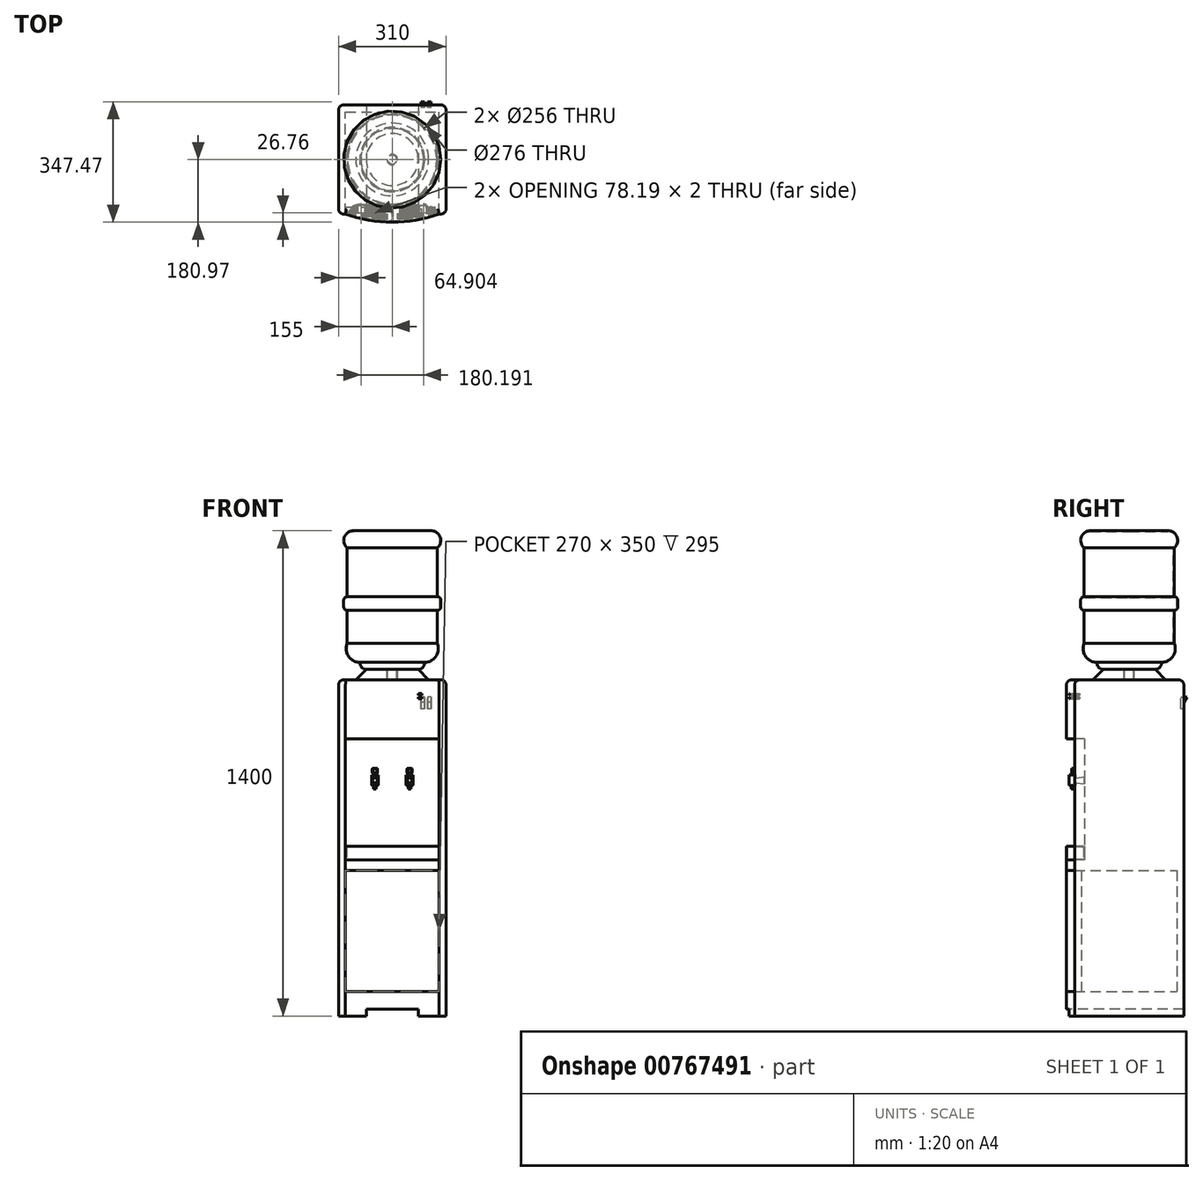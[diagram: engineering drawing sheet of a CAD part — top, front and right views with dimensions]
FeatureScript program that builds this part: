
annotation { "Feature Type Name" : "Feature", "Feature Type Description" : "" }
export const myFeature = defineFeature(function(context is Context, id is Id, definition is map)
    precondition{}
    {
        {
            var Q0;
            Q0=qCreatedBy(makeId("Top.planeOp"),FACE);
            var sketch = newSketch(context, id + "F0", { "sketchPlane" : qUnion([Q0])});
            skLineSegment(sketch, "E0.bottom", {"start": v(155, -157.5) * mm, "end": v(-155, -157.5) * mm});
            skLineSegment(sketch, "E0.top", {"start": v(155, 157.5) * mm, "end": v(-155, 157.5) * mm});
            skLineSegment(sketch, "E0.left", {"start": v(155, -157.5) * mm, "end": v(155, 157.5) * mm});
            skLineSegment(sketch, "E0.right", {"start": v(-155, -157.5) * mm, "end": v(-155, 157.5) * mm});
            skPoint(sketch, "E0.middle", {"position": v(0, 0) * mm});
            skArc(sketch, "E1", {"start": v(-135, -157.5) * mm, "mid": v(0, -180.97) * mm, "end": v(135, -157.5) * mm});
            skSolve(sketch);
        }
        {
            var Q0;
            Q0=makeQuery(id+"F0.imprint","IMPRINT",FACE,{"disambiguationData":[TD([[makeQuery(id+"F0.imprint","IMPRINT",EDGE,{"derivedFrom":sQuery(id+"F0.wireOp",EDGE,"E0.bottom")}),-1.0]])]});
            var Q1;
            {var subQ0=sQuery(id+"F0.wireOp",EDGE,"E1");Q1=makeQuery(id+"F0.imprint","IMPRINT",FACE,{"disambiguationData":[TD([[makeQuery(id+"F0.imprint","IMPRINT",EDGE,{"derivedFrom":subQ0}),1.0]])]});}
            extrude(context, id + "F1", {"entities" : qUnion([Q0, Q1]), "depth" : 970 * mm, "offsetDistance" : 25 * mm});
        }
        {
            var Q0;
            Q0=qCreatedBy(makeId("Front.planeOp"),FACE);
            var sketch = newSketch(context, id + "F2", { "sketchPlane" : qUnion([Q0])});
            skLineSegment(sketch, "E2.0", {"start": v(155, 970) * mm, "end": v(-155, 970) * mm});
            skLineSegment(sketch, "E3", {"start": v(105, 970) * mm, "end": v(75, 1000) * mm});
            skLineSegment(sketch, "E4", {"start": v(75, 1000) * mm, "end": v(0, 1000) * mm});
            skLineSegment(sketch, "E5", {"start": v(0, 1000) * mm, "end": v(0, 970) * mm});
            skLineSegment(sketch, "E6", {"start": v(15, 1000) * mm, "end": v(15, 970) * mm});
            skSolve(sketch);
        }
        {
            var Q0;
            {var subQ0=sQuery(id+"F2.wireOp",EDGE,"E3");Q0=makeQuery(id+"F2.imprint","IMPRINT",FACE,{"disambiguationData":[TD([[makeQuery(id+"F2.imprint","IMPRINT",EDGE,{"derivedFrom":subQ0}),1.0]])]});}
            var Q1;
            Q1=sQuery(id+"F2.wireOp",EDGE,"E5");
            revolve(context, id + "F3", {"operationType" : NewBodyOperationType.ADD, "surfaceOperationType" : NewSurfaceOperationType.NEW, "entities" : qUnion([Q0]), "axis" : qUnion([Q1]), "revolveType" : RevolveType.FULL});
        }
        {
            var Q0;
            Q0=qCreatedBy(makeId("Top.planeOp"),FACE);
            cPlane(context, id + "F4", {"entities" : qUnion([Q0]), "cplaneType" : CPlaneType.OFFSET, "offset" : 450 * mm, "width" : 150 * mm, "height" : 150 * mm});
        }
        {
            var Q0;
            Q0=qCreatedBy(id+"F4.planeOp",FACE);
            var sketch = newSketch(context, id + "F5", { "sketchPlane" : qUnion([Q0])});
            skArc(sketch, "E7.0.0", {"start": v(-135, -157.5) * mm, "mid": v(0, -180.97) * mm, "end": v(135, -157.5) * mm});
            skArc(sketch, "E7.0.2", {"start": v(135, -157.5) * mm, "mid": v(0, -180.97) * mm, "end": v(-135, -157.5) * mm});
            skLineSegment(sketch, "E8", {"start": v(-90, -129.3) * mm, "end": v(0, -129.3) * mm});
            skArc(sketch, "E9", {"start": v(-90, -129.3) * mm, "mid": v(-116.55, -136.93) * mm, "end": v(-135, -157.5) * mm});
            skLineSegment(sketch, "E10.MirrorCS", {"start": v(90, -129.3) * mm, "end": v(0, -129.3) * mm});
            skArc(sketch, "E11.MirrorCS", {"start": v(90, -129.3) * mm, "mid": v(116.55, -136.93) * mm, "end": v(135, -157.5) * mm});
            skSolve(sketch);
        }
        {
            var Q0;
            Q0=qSketchRegion(id+"F5",true);
            extrude(context, id + "F6", {"entities" : qUnion([Q0]), "operationType" : NewBodyOperationType.REMOVE, "depth" : 350 * mm, "offsetDistance" : 25 * mm});
        }
        {
            var Q0;
            Q0=qCreatedBy(makeId("Front.planeOp"),FACE);
            var sketch = newSketch(context, id + "F7", { "sketchPlane" : qUnion([Q0])});
            skLineSegment(sketch, "E12.0", {"start": v(-135, 450) * mm, "end": v(-135, 0) * mm});
            skLineSegment(sketch, "E12.1", {"start": v(135, 450) * mm, "end": v(135, 0) * mm});
            skLineSegment(sketch, "E13", {"start": v(-135, 420) * mm, "end": v(135, 420) * mm});
            skLineSegment(sketch, "E14", {"start": v(-135, 70) * mm, "end": v(135, 70) * mm});
            skSolve(sketch);
        }
        {
            var Q0;
            Q0=qSketchRegion(id+"F7",true);
            extrude(context, id + "F8", {"entities" : qUnion([Q0]), "operationType" : NewBodyOperationType.REMOVE, "endBound" : BoundingType.THROUGH_ALL, "depth" : 25 * mm, "offsetDistance" : 25 * mm, "hasSecondDirection" : true, "secondDirectionOppositeDirection" : true, "secondDirectionDepth" : (315 / 2 - 20) * mm});
        }
        {
            var Q0;
            Q0=qCreatedBy(makeId("Front.planeOp"),FACE);
            var sketch = newSketch(context, id + "F9", { "sketchPlane" : qUnion([Q0])});
            skLineSegment(sketch, "E15.bottom", {"start": v(-75, 20) * mm, "end": v(75, 20) * mm});
            skLineSegment(sketch, "E15.top", {"start": v(-75, 0) * mm, "end": v(75, 0) * mm});
            skLineSegment(sketch, "E15.left", {"start": v(-75, 20) * mm, "end": v(-75, 0) * mm});
            skLineSegment(sketch, "E15.right", {"start": v(75, 20) * mm, "end": v(75, 0) * mm});
            skSolve(sketch);
        }
        {
            var Q0;
            Q0=qSketchRegion(id+"F9",true);
            extrude(context, id + "F10", {"entities" : qUnion([Q0]), "operationType" : NewBodyOperationType.REMOVE, "endBound" : BoundingType.THROUGH_ALL, "oppositeDirection" : true, "depth" : 25 * mm, "offsetDistance" : 25 * mm, "hasSecondDirection" : true, "secondDirectionBound" : BoundingType.THROUGH_ALL, "secondDirectionOppositeDirection" : false, "secondDirectionDepth" : 25 * mm});
        }
        {
            var Q0;
            Q0=qCreatedBy(makeId("Front.planeOp"),FACE);
            var sketch = newSketch(context, id + "F11", { "sketchPlane" : qUnion([Q0])});
            skLineSegment(sketch, "E16.0", {"start": v(-15, 1000) * mm, "end": v(15, 1000) * mm});
            skLineSegment(sketch, "E17.0.0", {"start": v(-15, 970) * mm, "end": v(15, 970) * mm});
            skLineSegment(sketch, "E18", {"start": v(-15, 970) * mm, "end": v(-15, 1000) * mm});
            skLineSegment(sketch, "E19", {"start": v(0, 1400) * mm, "end": v(-112, 1400) * mm});
            skLineSegment(sketch, "E20", {"start": v(-130, 1350.55) * mm, "end": v(-130, 1210) * mm});
            skLineSegment(sketch, "E21", {"start": v(-130, 1170) * mm, "end": v(-130, 1075) * mm});
            skLineSegment(sketch, "E22.0", {"start": v(-75, 1000) * mm, "end": v(75, 1000) * mm});
            skArc(sketch, "E23", {"start": v(-92.88, 1020.1) * mm, "mid": v(-88.45, 1006.04) * mm, "end": v(-75, 1000) * mm});
            skLineSegment(sketch, "E24", {"start": v(-140, 1200) * mm, "end": v(-140, 1180) * mm});
            skArc(sketch, "E25", {"start": v(-140, 1180) * mm, "mid": v(-137.07, 1172.93) * mm, "end": v(-130, 1170) * mm});
            skLineSegment(sketch, "E26", {"start": v(-140, 1180) * mm, "end": v(-130, 1180) * mm, "construction": true});
            skLineSegment(sketch, "E27", {"start": v(-130, 1170) * mm, "end": v(-130, 1180) * mm, "construction": true});
            skArc(sketch, "E28", {"start": v(-112, 1400) * mm, "mid": v(-138.31, 1381.58) * mm, "end": v(-130, 1350.55) * mm});
            skArc(sketch, "E29", {"start": v(-130, 1210) * mm, "mid": v(-137.07, 1207.07) * mm, "end": v(-140, 1200) * mm});
            skLineSegment(sketch, "E30", {"start": v(-140, 1200) * mm, "end": v(-130, 1200) * mm, "construction": true});
            skLineSegment(sketch, "E31", {"start": v(-130, 1210) * mm, "end": v(-130, 1200) * mm, "construction": true});
            skArc(sketch, "E32", {"start": v(-130, 1075) * mm, "mid": v(-126.01, 1037.7) * mm, "end": v(-92.88, 1020.1) * mm});
            skLineSegment(sketch, "E33", {"start": v(-92.88, 1020.1) * mm, "end": v(0, 1020.1) * mm});
            skLineSegment(sketch, "E34", {"start": v(0, 1400) * mm, "end": v(0, 970) * mm});
            skLineSegment(sketch, "E35.0", {"start": v(-75, 1002) * mm, "end": v(75, 1002) * mm});
            skArc(sketch, "E35.1", {"start": v(-90.44, 1022.18) * mm, "mid": v(-87.7, 1008.28) * mm, "end": v(-75, 1002) * mm});
            skArc(sketch, "E35.2", {"start": v(-128, 1074.6) * mm, "mid": v(-123.77, 1037.98) * mm, "end": v(-90.44, 1022.18) * mm});
            skLineSegment(sketch, "E35.3", {"start": v(-128, 1172.25) * mm, "end": v(-128, 1074.6) * mm});
            skArc(sketch, "E35.4", {"start": v(-138, 1180) * mm, "mid": v(-134.9, 1173.68) * mm, "end": v(-128, 1172.25) * mm});
            skLineSegment(sketch, "E35.5", {"start": v(-138, 1200) * mm, "end": v(-138, 1180) * mm});
            skLineSegment(sketch, "E35.6", {"start": v(0, 1398) * mm, "end": v(-112, 1398) * mm});
            skArc(sketch, "E35.7", {"start": v(-112, 1398) * mm, "mid": v(-136.58, 1380.46) * mm, "end": v(-128, 1351.5) * mm});
            skLineSegment(sketch, "E35.8", {"start": v(-128, 1351.5) * mm, "end": v(-128, 1207.75) * mm});
            skArc(sketch, "E35.9", {"start": v(-128, 1207.75) * mm, "mid": v(-134.9, 1206.32) * mm, "end": v(-138, 1200) * mm});
            skLineSegment(sketch, "E36", {"start": v(-13, 970) * mm, "end": v(-13, 1002) * mm});
            skSolve(sketch);
        }
        {
            var Q0;
            {var subQ3=sQuery(id+"F11.wireOp",EDGE,"E18");Q0=makeQuery(id+"F11.imprint","IMPRINT",FACE,{"disambiguationData":[TD([[makeQuery(id+"F11.imprint","IMPRINT",EDGE,{"derivedFrom":subQ3}),-1.0]])]});}
            var Q1;
            {var subQ0=sQuery(id+"F11.wireOp",EDGE,"E23");Q1=makeQuery(id+"F11.imprint","IMPRINT",FACE,{"disambiguationData":[TD([[makeQuery(id+"F11.imprint","IMPRINT",EDGE,{"derivedFrom":subQ0}),1.0]])]});}
            var Q2;
            {var subQ4=sQuery(id+"F11.wireOp",EDGE,"E19");Q2=makeQuery(id+"F11.imprint","IMPRINT",FACE,{"disambiguationData":[TD([[makeQuery(id+"F11.imprint","IMPRINT",EDGE,{"derivedFrom":subQ4}),1.0]])]});}
            var Q3;
            Q3=sQuery(id+"F11.wireOp",EDGE,"E34");
            revolve(context, id + "F12", {"surfaceOperationType" : NewSurfaceOperationType.NEW, "entities" : qUnion([Q0, Q1, Q2]), "axis" : qUnion([Q3]), "revolveType" : RevolveType.FULL});
        }
        {
            var Q0;
            Q0=makeQuery(id+"F1.opExtrude","SWEPT_EDGE",EDGE,{"disambiguationData":[OSD([sQuery(id+"F0.wireOp",EDGE,"E0.top"),sQuery(id+"F0.wireOp",EDGE,"E0.right")])]});
            var Q1;
            Q1=makeQuery(id+"F1.opExtrude","SWEPT_EDGE",EDGE,{"disambiguationData":[OSD([sQuery(id+"F0.wireOp",EDGE,"E0.bottom"),sQuery(id+"F0.wireOp",EDGE,"E0.right")])]});
            var Q2;
            Q2=makeQuery(id+"F1.opExtrude","SWEPT_EDGE",EDGE,{"disambiguationData":[OSD([sQuery(id+"F0.wireOp",EDGE,"E0.bottom"),sQuery(id+"F0.wireOp",EDGE,"E0.left")])]});
            var Q3;
            Q3=makeQuery(id+"F1.opExtrude","SWEPT_EDGE",EDGE,{"disambiguationData":[OSD([sQuery(id+"F0.wireOp",EDGE,"E0.top"),sQuery(id+"F0.wireOp",EDGE,"E0.left")])]});
            var Q4;
            Q4=makeQuery(id+"F1.opExtrude","CAP_EDGE",EDGE,{"disambiguationData":[OSD([sQuery(id+"F0.wireOp",EDGE,"E0.top")])],"isStart":false});
            var Q5;
            Q5=makeQuery(id+"F1.opExtrude","CAP_EDGE",EDGE,{"disambiguationData":[OSD([sQuery(id+"F0.wireOp",EDGE,"E0.left")])],"isStart":false});
            var Q6;
            Q6=makeQuery(id+"F1.opExtrude","CAP_EDGE",EDGE,{"disambiguationData":[OSD([sQuery(id+"F0.wireOp",EDGE,"E0.right")])],"isStart":false});
            var Q7;
            Q7=makeQuery(id+"F1.opExtrude","CAP_EDGE",EDGE,{"disambiguationData":[OSD([sQuery(id+"F0.wireOp",EDGE,"E1")])],"isStart":false});
            var Q8;
            {var subQ0=sQuery(id+"F0.wireOp",EDGE,"E0.bottom");Q8=makeQuery(id+"F1.opExtrude","CAP_EDGE",EDGE,{"disambiguationData":[OSD([subQ0]),TDD([makeQuery(id+"F0.imprint","IMPRINT",EDGE,{"disambiguationData":[TD([[makeQuery(id+"F0.imprint","INTERSECT",VERTEX,{"derivedFrom":[subQ0,sQuery(id+"F0.wireOp",EDGE,"E0.right")]}),1.0]])],"derivedFrom":subQ0})])],"isStart":false});}
            var Q9;
            {var subQ0=sQuery(id+"F0.wireOp",EDGE,"E0.bottom");Q9=makeQuery(id+"F1.opExtrude","CAP_EDGE",EDGE,{"disambiguationData":[OSD([subQ0]),TDD([makeQuery(id+"F0.imprint","IMPRINT",EDGE,{"disambiguationData":[TD([[makeQuery(id+"F0.imprint","INTERSECT",VERTEX,{"derivedFrom":[subQ0,sQuery(id+"F0.wireOp",EDGE,"E0.left")]}),-1.0]])],"derivedFrom":subQ0})])],"isStart":false});}
            fillet(context, id + "F13", {"entities" : qUnion([Q0, Q1, Q2, Q3, Q4, Q5, Q6, Q7, Q8, Q9]), "radius" : 15 * mm, "tangentPropagation" : true, "allowEdgeOverflow" : false});
        }
        {
            var Q0;
            Q0=makeQuery(id+"F6.boolean.opBoolean","COPY",FACE,{"derivedFrom":makeQuery(id+"F6.opExtrude","CAP_FACE",FACE,{"disambiguationData":[OSD([sQuery(id+"F5.wireOp",EDGE,"E7.0.2"),sQuery(id+"F5.wireOp",EDGE,"E8"),sQuery(id+"F5.wireOp",EDGE,"E9"),sQuery(id+"F5.wireOp",EDGE,"E10.MirrorCS"),sQuery(id+"F5.wireOp",EDGE,"E11.MirrorCS")])],"isStart":true})});
            var sketch = newSketch(context, id + "F14", { "sketchPlane" : qUnion([Q0])});
            skArc(sketch, "E37.0", {"start": v(-90, -129.3) * mm, "mid": v(-116.55, -136.93) * mm, "end": v(-135, -157.5) * mm});
            skLineSegment(sketch, "E37.1", {"start": v(90, -129.3) * mm, "end": v(-90, -129.3) * mm});
            skArc(sketch, "E37.2", {"start": v(90, -129.3) * mm, "mid": v(116.55, -136.93) * mm, "end": v(135, -157.5) * mm});
            skArc(sketch, "E37.3", {"start": v(135, -157.5) * mm, "mid": v(0, -180.97) * mm, "end": v(-135, -157.5) * mm});
            skSolve(sketch);
        }
        {
            var Q0;
            Q0=makeQuery(id+"F14.imprint","IMPRINT",FACE,{"disambiguationData":[TD([[makeQuery(id+"F14.imprint","IMPRINT",EDGE,{"derivedFrom":sQuery(id+"F14.wireOp",EDGE,"E37.0")}),1.0]])]});
            var Q1;
            Q1=qConstructionFilter(qBodyType(qCreatedBy(id+"F14",EDGE),BodyType.WIRE),ConstructionObject.NO);
            extrude(context, id + "F15", {"entities" : qUnion([Q0]), "surfaceEntities" : qUnion([Q1]), "depth" : 40 * mm, "offsetDistance" : 25 * mm});
        }
        {
            var Q0;
            Q0=makeQuery(id+"F15.opExtrude","CAP_FACE",FACE,{"disambiguationData":[OSD([sQuery(id+"F14.wireOp",EDGE,"E37.0"),sQuery(id+"F14.wireOp",EDGE,"E37.1"),sQuery(id+"F14.wireOp",EDGE,"E37.2"),sQuery(id+"F14.wireOp",EDGE,"E37.3")])],"isStart":false});
            shell(context, id + "F16", {"entities" : qUnion([Q0]), "thickness" : 2 * mm});
        }
        {
            var Q0;
            Q0=makeQuery(id+"F15.opExtrude","CAP_FACE",FACE,{"disambiguationData":[OSD([sQuery(id+"F14.wireOp",EDGE,"E37.0"),sQuery(id+"F14.wireOp",EDGE,"E37.1"),sQuery(id+"F14.wireOp",EDGE,"E37.2"),sQuery(id+"F14.wireOp",EDGE,"E37.3")])],"isStart":false});
            var sketch = newSketch(context, id + "F17", { "sketchPlane" : qUnion([Q0])});
            skArc(sketch, "E38.0", {"start": v(-90, -131.3) * mm, "mid": v(-114.54, -138.04) * mm, "end": v(-132.18, -156.38) * mm});
            skLineSegment(sketch, "E38.1", {"start": v(90, -131.3) * mm, "end": v(-90, -131.3) * mm});
            skArc(sketch, "E38.2", {"start": v(132.18, -156.38) * mm, "mid": v(0, -178.97) * mm, "end": v(-132.18, -156.38) * mm});
            skArc(sketch, "E38.3", {"start": v(90, -131.3) * mm, "mid": v(114.54, -138.04) * mm, "end": v(132.18, -156.38) * mm});
            skLineSegment(sketch, "E39.0", {"start": v(90, -133.3) * mm, "end": v(-90, -133.3) * mm});
            skArc(sketch, "E39.1", {"start": v(90, -133.3) * mm, "mid": v(112.5, -139.17) * mm, "end": v(129.24, -155.29) * mm});
            skArc(sketch, "E39.2", {"start": v(129.24, -155.29) * mm, "mid": v(0, -176.97) * mm, "end": v(-129.24, -155.29) * mm});
            skArc(sketch, "E39.3", {"start": v(-90, -133.3) * mm, "mid": v(-112.5, -139.17) * mm, "end": v(-129.24, -155.29) * mm});
            skLineSegment(sketch, "E40", {"start": v(0, -112.71) * mm, "end": v(0, -215.15) * mm, "construction": true});
            skLineSegment(sketch, "E41", {"start": v(-50, -106.6) * mm, "end": v(-50, -205.9) * mm, "construction": true});
            skLineSegment(sketch, "E42.bottom", {"start": v(-57.5, -156.3) * mm, "end": v(-42.5, -156.3) * mm});
            skLineSegment(sketch, "E42.top", {"start": v(-57.5, -171.3) * mm, "end": v(-42.5, -171.3) * mm});
            skLineSegment(sketch, "E42.left", {"start": v(-57.5, -156.3) * mm, "end": v(-57.5, -171.3) * mm});
            skLineSegment(sketch, "E42.right", {"start": v(-42.5, -156.3) * mm, "end": v(-42.5, -171.3) * mm});
            skLineSegment(sketch, "E43", {"start": v(-51, -156.3) * mm, "end": v(-51, -133.3) * mm});
            skLineSegment(sketch, "E44.MirrorCS", {"start": v(-49, -156.3) * mm, "end": v(-49, -133.3) * mm});
            skLineSegment(sketch, "E45", {"start": v(-51, -171.3) * mm, "end": v(-51, -173.67) * mm});
            skLineSegment(sketch, "E46", {"start": v(-49, -171.3) * mm, "end": v(-49, -173.93) * mm});
            skLineSegment(sketch, "E47", {"start": v(-1, -133.3) * mm, "end": v(-1, -176.97) * mm});
            skLineSegment(sketch, "E48", {"start": v(1, -133.3) * mm, "end": v(1, -176.97) * mm});
            skLineSegment(sketch, "E49", {"start": v(-49, -135.21) * mm, "end": v(-1, -135.21) * mm});
            skLineSegment(sketch, "E50.0.1.0", {"start": v(-49, -137.21) * mm, "end": v(-1, -137.21) * mm});
            skLineSegment(sketch, "E50.0.2.0", {"start": v(-49, -139.21) * mm, "end": v(-1, -139.21) * mm});
            skLineSegment(sketch, "E50.0.3.0", {"start": v(-49, -141.21) * mm, "end": v(-1, -141.21) * mm});
            skLineSegment(sketch, "E50.0.4.0", {"start": v(-49, -143.21) * mm, "end": v(-1, -143.21) * mm});
            skLineSegment(sketch, "E50.0.5.0", {"start": v(-49, -145.21) * mm, "end": v(-1, -145.21) * mm});
            skLineSegment(sketch, "E50.0.6.0", {"start": v(-49, -147.21) * mm, "end": v(-1, -147.21) * mm});
            skLineSegment(sketch, "E50.0.7.0", {"start": v(-49, -149.21) * mm, "end": v(-1, -149.21) * mm});
            skLineSegment(sketch, "E50.0.8.0", {"start": v(-49, -151.21) * mm, "end": v(-1, -151.21) * mm});
            skLineSegment(sketch, "E50.0.9.0", {"start": v(-49, -153.21) * mm, "end": v(-1, -153.21) * mm});
            skLineSegment(sketch, "E50.0.10.0", {"start": v(-49, -155.21) * mm, "end": v(-1, -155.21) * mm});
            skLineSegment(sketch, "E50.0.11.0", {"start": v(-42.5, -157.21) * mm, "end": v(-1, -157.21) * mm});
            skLineSegment(sketch, "E50.0.12.0", {"start": v(-44.5, -159.21) * mm, "end": v(-1, -159.21) * mm});
            skLineSegment(sketch, "E50.0.13.0", {"start": v(-44.5, -161.21) * mm, "end": v(-1, -161.21) * mm});
            skLineSegment(sketch, "E50.0.14.0", {"start": v(-44.5, -163.21) * mm, "end": v(-1, -163.21) * mm});
            skLineSegment(sketch, "E50.0.15.0", {"start": v(-49, -165.21) * mm, "end": v(-1, -165.21) * mm});
            skLineSegment(sketch, "E50.0.16.0", {"start": v(-49, -167.21) * mm, "end": v(-1, -167.21) * mm});
            skLineSegment(sketch, "E50.0.17.0", {"start": v(-49, -169.21) * mm, "end": v(-1, -169.21) * mm});
            skLineSegment(sketch, "E50.0.18.0", {"start": v(-49, -171.21) * mm, "end": v(-1, -171.21) * mm});
            skLineSegment(sketch, "E50.0.19.0", {"start": v(-49, -173.21) * mm, "end": v(-1, -173.21) * mm});
            skLineSegment(sketch, "E50.0.20.0", {"start": v(-49, -175.21) * mm, "end": v(-1, -175.21) * mm});
            skLineSegment(sketch, "E50.direction1", {"start": v(-49, -135.21) * mm, "end": v(-24, -135.21) * mm, "construction": true});
            skLineSegment(sketch, "E50.direction2", {"start": v(-49, -135.21) * mm, "end": v(-49, -137.21) * mm, "construction": true});
            skLineSegment(sketch, "E51.MirrorCS", {"start": v(-51, -137.21) * mm, "end": v(-108.57, -137.21) * mm});
            skLineSegment(sketch, "E52.MirrorCS", {"start": v(-51, -139.21) * mm, "end": v(-112.57, -139.21) * mm});
            skLineSegment(sketch, "E53.MirrorCS", {"start": v(-51, -141.21) * mm, "end": v(-115.8, -141.21) * mm});
            skLineSegment(sketch, "E54.MirrorCS", {"start": v(-51, -143.21) * mm, "end": v(-118.53, -143.21) * mm});
            skLineSegment(sketch, "E55.MirrorCS", {"start": v(-51, -145.21) * mm, "end": v(-120.9, -145.21) * mm});
            skLineSegment(sketch, "E56.MirrorCS", {"start": v(-51, -147.21) * mm, "end": v(-122.96, -147.21) * mm});
            skLineSegment(sketch, "E57.MirrorCS", {"start": v(-51, -149.21) * mm, "end": v(-124.8, -149.21) * mm});
            skLineSegment(sketch, "E58.MirrorCS", {"start": v(-51, -151.21) * mm, "end": v(-126.43, -151.21) * mm});
            skLineSegment(sketch, "E59.MirrorCS", {"start": v(-51, -153.21) * mm, "end": v(-127.89, -153.21) * mm});
            skLineSegment(sketch, "E60.MirrorCS", {"start": v(-51, -155.21) * mm, "end": v(-129.2, -155.21) * mm});
            skLineSegment(sketch, "E61.MirrorCS", {"start": v(-57.5, -157.21) * mm, "end": v(-123.53, -157.21) * mm});
            skLineSegment(sketch, "E62.MirrorCS", {"start": v(-57.5, -159.21) * mm, "end": v(-117.26, -159.21) * mm});
            skLineSegment(sketch, "E63.MirrorCS", {"start": v(-57.5, -161.21) * mm, "end": v(-110.6, -161.21) * mm});
            skLineSegment(sketch, "E64.MirrorCS", {"start": v(-57.5, -163.21) * mm, "end": v(-103.48, -163.21) * mm});
            skLineSegment(sketch, "E65.MirrorCS", {"start": v(-49, -165.21) * mm, "end": v(-50, -165.21) * mm});
            skLineSegment(sketch, "E66.MirrorCS", {"start": v(-57.5, -167.21) * mm, "end": v(-99, -167.21) * mm});
            skLineSegment(sketch, "E67.MirrorCS", {"start": v(-57.5, -169.21) * mm, "end": v(-99, -169.21) * mm});
            skLineSegment(sketch, "E68.MirrorCS", {"start": v(-51, -171.21) * mm, "end": v(-99, -171.21) * mm});
            skLineSegment(sketch, "E69.MirrorCS", {"start": v(-51, -173.21) * mm, "end": v(-99, -173.21) * mm});
            skPoint(sketch, "E70.orphan", {"position": v(-99, -137.21) * mm});
            skPoint(sketch, "E71.orphan", {"position": v(-99, -139.21) * mm});
            skPoint(sketch, "E72.orphan", {"position": v(-99, -141.21) * mm});
            skPoint(sketch, "E73.orphan", {"position": v(-99, -143.21) * mm});
            skPoint(sketch, "E74.orphan", {"position": v(-99, -145.21) * mm});
            skPoint(sketch, "E75.orphan", {"position": v(-99, -147.21) * mm});
            skPoint(sketch, "E76.orphan", {"position": v(-99, -149.21) * mm});
            skPoint(sketch, "E77.orphan", {"position": v(-99, -151.21) * mm});
            skPoint(sketch, "E78.orphan", {"position": v(-99, -153.21) * mm});
            skPoint(sketch, "E79.orphan", {"position": v(-99, -155.21) * mm});
            skPoint(sketch, "E80.orphan", {"position": v(-99, -157.21) * mm});
            skPoint(sketch, "E81.orphan", {"position": v(-99, -159.21) * mm});
            skPoint(sketch, "E82.orphan", {"position": v(-99, -161.21) * mm});
            skPoint(sketch, "E83.orphan", {"position": v(-99, -163.21) * mm});
            skLineSegment(sketch, "E84", {"start": v(-51, -135.21) * mm, "end": v(-103.14, -135.21) * mm});
            skLineSegment(sketch, "E85.0", {"start": v(-55.5, -158.3) * mm, "end": v(-44.5, -158.3) * mm});
            skLineSegment(sketch, "E85.1", {"start": v(-55.5, -158.3) * mm, "end": v(-55.5, -169.3) * mm});
            skLineSegment(sketch, "E85.2", {"start": v(-55.5, -169.3) * mm, "end": v(-44.5, -169.3) * mm});
            skLineSegment(sketch, "E85.3", {"start": v(-44.5, -158.3) * mm, "end": v(-44.5, -169.3) * mm});
            skPoint(sketch, "E86.orphan", {"position": v(-51, -157.21) * mm});
            skPoint(sketch, "E87.orphan", {"position": v(-51, -161.21) * mm});
            skPoint(sketch, "E88.orphan", {"position": v(-51, -165.21) * mm});
            skPoint(sketch, "E89.orphan", {"position": v(-51, -159.21) * mm});
            skPoint(sketch, "E90.orphan", {"position": v(-51, -163.21) * mm});
            skLineSegment(sketch, "E91.trimOffspring", {"start": v(-57.5, -165.21) * mm, "end": v(-99, -165.21) * mm});
            skPoint(sketch, "E92.orphan", {"position": v(-51, -167.21) * mm});
            skPoint(sketch, "E93.orphan", {"position": v(-51, -169.21) * mm});
            skPoint(sketch, "E94.orphan", {"position": v(-49, -159.21) * mm});
            skPoint(sketch, "E95.orphan", {"position": v(-49, -157.21) * mm});
            skPoint(sketch, "E96.orphan", {"position": v(-49, -161.21) * mm});
            skPoint(sketch, "E97.orphan", {"position": v(-49, -163.21) * mm});
            skLineSegment(sketch, "E98.MirrorCS", {"start": v(49, -165.21) * mm, "end": v(1, -165.21) * mm});
            skLineSegment(sketch, "E99.MirrorCS", {"start": v(44.5, -163.21) * mm, "end": v(1, -163.21) * mm});
            skLineSegment(sketch, "E100.MirrorCS", {"start": v(49, -167.21) * mm, "end": v(1, -167.21) * mm});
            skLineSegment(sketch, "E101.MirrorCS", {"start": v(44.5, -159.21) * mm, "end": v(1, -159.21) * mm});
            skLineSegment(sketch, "E102.MirrorCS", {"start": v(49, -171.21) * mm, "end": v(1, -171.21) * mm});
            skLineSegment(sketch, "E103.MirrorCS", {"start": v(42.5, -157.21) * mm, "end": v(1, -157.21) * mm});
            skLineSegment(sketch, "E104.MirrorCS", {"start": v(49, -175.21) * mm, "end": v(1, -175.21) * mm});
            skLineSegment(sketch, "E105.MirrorCS", {"start": v(49, -173.21) * mm, "end": v(1, -173.21) * mm});
            skLineSegment(sketch, "E106.MirrorCS", {"start": v(44.5, -161.21) * mm, "end": v(1, -161.21) * mm});
            skLineSegment(sketch, "E107.MirrorCS", {"start": v(49, -169.21) * mm, "end": v(1, -169.21) * mm});
            skLineSegment(sketch, "E108.MirrorCS", {"start": v(49, -135.21) * mm, "end": v(1, -135.21) * mm});
            skLineSegment(sketch, "E109.MirrorCS", {"start": v(49, -145.21) * mm, "end": v(1, -145.21) * mm});
            skLineSegment(sketch, "E110.MirrorCS", {"start": v(49, -137.21) * mm, "end": v(1, -137.21) * mm});
            skLineSegment(sketch, "E111.MirrorCS", {"start": v(49, -143.21) * mm, "end": v(1, -143.21) * mm});
            skLineSegment(sketch, "E112.MirrorCS", {"start": v(49, -153.21) * mm, "end": v(1, -153.21) * mm});
            skLineSegment(sketch, "E113.MirrorCS", {"start": v(49, -141.21) * mm, "end": v(1, -141.21) * mm});
            skLineSegment(sketch, "E114.MirrorCS", {"start": v(49, -151.21) * mm, "end": v(1, -151.21) * mm});
            skLineSegment(sketch, "E115.MirrorCS", {"start": v(49, -149.21) * mm, "end": v(1, -149.21) * mm});
            skLineSegment(sketch, "E116.MirrorCS", {"start": v(49, -147.21) * mm, "end": v(1, -147.21) * mm});
            skLineSegment(sketch, "E117.MirrorCS", {"start": v(49, -139.21) * mm, "end": v(1, -139.21) * mm});
            skLineSegment(sketch, "E118.MirrorCS", {"start": v(49, -155.21) * mm, "end": v(1, -155.21) * mm});
            skLineSegment(sketch, "E119.MirrorCS", {"start": v(42.5, -156.3) * mm, "end": v(42.5, -171.3) * mm});
            skLineSegment(sketch, "E120.MirrorCS", {"start": v(44.5, -158.3) * mm, "end": v(44.5, -169.3) * mm});
            skLineSegment(sketch, "E121.MirrorCS", {"start": v(55.5, -158.3) * mm, "end": v(55.5, -169.3) * mm});
            skLineSegment(sketch, "E122.MirrorCS", {"start": v(57.5, -156.3) * mm, "end": v(42.5, -156.3) * mm});
            skLineSegment(sketch, "E123.MirrorCS", {"start": v(51, -171.21) * mm, "end": v(99, -171.21) * mm});
            skLineSegment(sketch, "E124.MirrorCS", {"start": v(57.5, -156.3) * mm, "end": v(57.5, -171.3) * mm});
            skLineSegment(sketch, "E125.MirrorCS", {"start": v(57.5, -171.3) * mm, "end": v(42.5, -171.3) * mm});
            skLineSegment(sketch, "E126.MirrorCS", {"start": v(49, -171.3) * mm, "end": v(49, -173.93) * mm});
            skLineSegment(sketch, "E127.MirrorCS", {"start": v(51, -171.3) * mm, "end": v(51, -173.67) * mm});
            skLineSegment(sketch, "E128.MirrorCS", {"start": v(51, -151.21) * mm, "end": v(126.43, -151.21) * mm});
            skLineSegment(sketch, "E129.MirrorCS", {"start": v(51, -155.21) * mm, "end": v(129.2, -155.21) * mm});
            skLineSegment(sketch, "E130.MirrorCS", {"start": v(57.5, -165.21) * mm, "end": v(99, -165.21) * mm});
            skLineSegment(sketch, "E131.MirrorCS", {"start": v(57.5, -157.21) * mm, "end": v(123.53, -157.21) * mm});
            skLineSegment(sketch, "E132.MirrorCS", {"start": v(51, -153.21) * mm, "end": v(127.89, -153.21) * mm});
            skLineSegment(sketch, "E133.MirrorCS", {"start": v(57.5, -159.21) * mm, "end": v(117.26, -159.21) * mm});
            skLineSegment(sketch, "E134.MirrorCS", {"start": v(57.5, -167.21) * mm, "end": v(99, -167.21) * mm});
            skLineSegment(sketch, "E135.MirrorCS", {"start": v(51, -141.21) * mm, "end": v(115.8, -141.21) * mm});
            skLineSegment(sketch, "E136.MirrorCS", {"start": v(51, -149.21) * mm, "end": v(124.8, -149.21) * mm});
            skLineSegment(sketch, "E137.MirrorCS", {"start": v(51, -147.21) * mm, "end": v(122.96, -147.21) * mm});
            skLineSegment(sketch, "E138.MirrorCS", {"start": v(51, -137.21) * mm, "end": v(108.57, -137.21) * mm});
            skLineSegment(sketch, "E139.MirrorCS", {"start": v(57.5, -169.21) * mm, "end": v(99, -169.21) * mm});
            skLineSegment(sketch, "E140.MirrorCS", {"start": v(51, -145.21) * mm, "end": v(120.9, -145.21) * mm});
            skLineSegment(sketch, "E141.MirrorCS", {"start": v(51, -139.21) * mm, "end": v(112.57, -139.21) * mm});
            skLineSegment(sketch, "E142.MirrorCS", {"start": v(51, -135.21) * mm, "end": v(103.14, -135.21) * mm});
            skLineSegment(sketch, "E143.MirrorCS", {"start": v(-90, -133.3) * mm, "end": v(90, -133.3) * mm});
            skLineSegment(sketch, "E144.MirrorCS", {"start": v(51, -143.21) * mm, "end": v(118.53, -143.21) * mm});
            skLineSegment(sketch, "E145.MirrorCS", {"start": v(57.5, -163.21) * mm, "end": v(103.48, -163.21) * mm});
            skLineSegment(sketch, "E146.MirrorCS", {"start": v(57.5, -161.21) * mm, "end": v(110.6, -161.21) * mm});
            skPoint(sketch, "E147.MirrorP", {"position": v(99, -145.21) * mm});
            skPoint(sketch, "E148.MirrorP", {"position": v(99, -141.21) * mm});
            skPoint(sketch, "E149.MirrorP", {"position": v(99, -143.21) * mm});
            skPoint(sketch, "E150.MirrorP", {"position": v(99, -139.21) * mm});
            skPoint(sketch, "E151.MirrorP", {"position": v(99, -137.21) * mm});
            skPoint(sketch, "E152.MirrorP", {"position": v(99, -155.21) * mm});
            skPoint(sketch, "E153.MirrorP", {"position": v(99, -147.21) * mm});
            skPoint(sketch, "E154.MirrorP", {"position": v(99, -149.21) * mm});
            skPoint(sketch, "E155.MirrorP", {"position": v(99, -157.21) * mm});
            skPoint(sketch, "E156.MirrorP", {"position": v(99, -151.21) * mm});
            skPoint(sketch, "E157.MirrorP", {"position": v(99, -153.21) * mm});
            skLineSegment(sketch, "E158.MirrorCS", {"start": v(55.5, -158.3) * mm, "end": v(44.5, -158.3) * mm});
            skLineSegment(sketch, "E159.MirrorCS", {"start": v(55.5, -169.3) * mm, "end": v(44.5, -169.3) * mm});
            skLineSegment(sketch, "E160.MirrorCS", {"start": v(51, -156.3) * mm, "end": v(51, -133.3) * mm});
            skLineSegment(sketch, "E161.MirrorCS", {"start": v(49, -156.3) * mm, "end": v(49, -133.3) * mm});
            skLineSegment(sketch, "E162.MirrorCS", {"start": v(51, -173.21) * mm, "end": v(99, -173.21) * mm});
            skSolve(sketch);
        }
        {
            var Q0;
            {var subQ16=sQuery(id+"F17.wireOp",EDGE,"E38.0");Q0=makeQuery(id+"F17.imprint","IMPRINT",FACE,{"disambiguationData":[TD([[makeQuery(id+"F17.imprint","IMPRINT",EDGE,{"derivedFrom":subQ16}),1.0]])]});}
            var Q1;
            {var subQ0=sQuery(id+"F17.wireOp",EDGE,"E66.MirrorCS");var subQ1=sQuery(id+"F17.wireOp",EDGE,"E38.2");var subQ2=makeQuery(id+"F17.imprint","INTERSECT",VERTEX,{"derivedFrom":[subQ1,subQ0]});Q1=makeQuery(id+"F17.imprint","IMPRINT",FACE,{"disambiguationData":[TD([[makeQuery(id+"F17.imprint","IMPRINT",EDGE,{"disambiguationData":[TD([[subQ2,1.0]])],"derivedFrom":subQ1}),-1.0]])]});}
            var Q2;
            {var subQ0=sQuery(id+"F17.wireOp",EDGE,"E67.MirrorCS");var subQ1=sQuery(id+"F17.wireOp",EDGE,"E38.2");var subQ2=makeQuery(id+"F17.imprint","INTERSECT",VERTEX,{"derivedFrom":[subQ1,subQ0]});Q2=makeQuery(id+"F17.imprint","IMPRINT",FACE,{"disambiguationData":[TD([[makeQuery(id+"F17.imprint","IMPRINT",EDGE,{"disambiguationData":[TD([[subQ2,1.0]])],"derivedFrom":subQ1}),-1.0]])]});}
            var Q3;
            {var subQ0=sQuery(id+"F17.wireOp",EDGE,"E68.MirrorCS");var subQ1=sQuery(id+"F17.wireOp",EDGE,"E38.2");var subQ2=makeQuery(id+"F17.imprint","INTERSECT",VERTEX,{"derivedFrom":[subQ1,subQ0]});Q3=makeQuery(id+"F17.imprint","IMPRINT",FACE,{"disambiguationData":[TD([[makeQuery(id+"F17.imprint","IMPRINT",EDGE,{"disambiguationData":[TD([[subQ2,1.0]])],"derivedFrom":subQ1}),-1.0]])]});}
            var Q4;
            {var subQ0=sQuery(id+"F17.wireOp",EDGE,"E134.MirrorCS");var subQ1=sQuery(id+"F17.wireOp",EDGE,"E38.2");var subQ2=makeQuery(id+"F17.imprint","INTERSECT",VERTEX,{"derivedFrom":[subQ1,subQ0]});Q4=makeQuery(id+"F17.imprint","IMPRINT",FACE,{"disambiguationData":[TD([[makeQuery(id+"F17.imprint","IMPRINT",EDGE,{"disambiguationData":[TD([[subQ2,-1.0]])],"derivedFrom":subQ1}),-1.0]])]});}
            var Q5;
            {var subQ0=sQuery(id+"F17.wireOp",EDGE,"E123.MirrorCS");var subQ1=sQuery(id+"F17.wireOp",EDGE,"E38.2");var subQ2=makeQuery(id+"F17.imprint","INTERSECT",VERTEX,{"derivedFrom":[subQ1,subQ0]});Q5=makeQuery(id+"F17.imprint","IMPRINT",FACE,{"disambiguationData":[TD([[makeQuery(id+"F17.imprint","IMPRINT",EDGE,{"disambiguationData":[TD([[subQ2,1.0]])],"derivedFrom":subQ1}),-1.0]])]});}
            var Q6;
            {var subQ7=sQuery(id+"F17.wireOp",EDGE,"E69.MirrorCS");var subQ9=sQuery(id+"F17.wireOp",EDGE,"E38.2");var subQ10=makeQuery(id+"F17.imprint","INTERSECT",VERTEX,{"derivedFrom":[subQ9,subQ7]});Q6=makeQuery(id+"F17.imprint","IMPRINT",FACE,{"disambiguationData":[TD([[makeQuery(id+"F17.imprint","IMPRINT",EDGE,{"disambiguationData":[TD([[subQ10,1.0]])],"derivedFrom":subQ9}),-1.0]])]});}
            var Q7;
            {var subQ0=sQuery(id+"F17.wireOp",EDGE,"E162.MirrorCS");var subQ1=sQuery(id+"F17.wireOp",EDGE,"E38.2");var subQ2=makeQuery(id+"F17.imprint","INTERSECT",VERTEX,{"derivedFrom":[subQ1,subQ0]});Q7=makeQuery(id+"F17.imprint","IMPRINT",FACE,{"disambiguationData":[TD([[makeQuery(id+"F17.imprint","IMPRINT",EDGE,{"disambiguationData":[TD([[subQ2,1.0]])],"derivedFrom":subQ1}),-1.0]])]});}
            extrude(context, id + "F18", {"entities" : qUnion([Q0, Q1, Q2, Q3, Q4, Q5, Q6, Q7]), "oppositeDirection" : true, "depth" : 2 * mm, "offsetDistance" : 25 * mm});
        }
        {
            var Q0;
            {var subQ0=sQuery(id+"F17.wireOp",EDGE,"E47");var subQ7=sQuery(id+"F17.wireOp",EDGE,"E39.2");var subQ8=makeQuery(id+"F17.imprint","INTERSECT",VERTEX,{"derivedFrom":[subQ7,subQ0]});Q0=makeQuery(id+"F17.imprint","IMPRINT",FACE,{"disambiguationData":[TD([[makeQuery(id+"F17.imprint","IMPRINT",EDGE,{"disambiguationData":[TD([[subQ8,1.0]])],"derivedFrom":subQ7}),-1.0]])]});}
            var Q1;
            {var subQ0=sQuery(id+"F17.wireOp",EDGE,"E49");Q1=makeQuery(id+"F17.imprint","IMPRINT",FACE,{"disambiguationData":[TD([[makeQuery(id+"F17.imprint","IMPRINT",EDGE,{"derivedFrom":subQ0}),-1.0]])]});}
            var Q2;
            {var subQ0=sQuery(id+"F17.wireOp",EDGE,"E50.0.2.0");Q2=makeQuery(id+"F17.imprint","IMPRINT",FACE,{"disambiguationData":[TD([[makeQuery(id+"F17.imprint","IMPRINT",EDGE,{"derivedFrom":subQ0}),-1.0]])]});}
            var Q3;
            {var subQ0=sQuery(id+"F17.wireOp",EDGE,"E50.0.4.0");Q3=makeQuery(id+"F17.imprint","IMPRINT",FACE,{"disambiguationData":[TD([[makeQuery(id+"F17.imprint","IMPRINT",EDGE,{"derivedFrom":subQ0}),-1.0]])]});}
            var Q4;
            {var subQ0=sQuery(id+"F17.wireOp",EDGE,"E50.0.6.0");Q4=makeQuery(id+"F17.imprint","IMPRINT",FACE,{"disambiguationData":[TD([[makeQuery(id+"F17.imprint","IMPRINT",EDGE,{"derivedFrom":subQ0}),-1.0]])]});}
            var Q5;
            {var subQ0=sQuery(id+"F17.wireOp",EDGE,"E50.0.8.0");Q5=makeQuery(id+"F17.imprint","IMPRINT",FACE,{"disambiguationData":[TD([[makeQuery(id+"F17.imprint","IMPRINT",EDGE,{"derivedFrom":subQ0}),-1.0]])]});}
            var Q6;
            {var subQ0=sQuery(id+"F17.wireOp",EDGE,"E50.0.10.0");Q6=makeQuery(id+"F17.imprint","IMPRINT",FACE,{"disambiguationData":[TD([[makeQuery(id+"F17.imprint","IMPRINT",EDGE,{"derivedFrom":subQ0}),-1.0]])]});}
            var Q7;
            {var subQ0=sQuery(id+"F17.wireOp",EDGE,"E50.0.12.0");var subQ1=sQuery(id+"F17.wireOp",EDGE,"E42.right");var subQ2=makeQuery(id+"F17.imprint","INTERSECT",VERTEX,{"derivedFrom":[subQ1,subQ0]});Q7=makeQuery(id+"F17.imprint","IMPRINT",FACE,{"disambiguationData":[TD([[makeQuery(id+"F17.imprint","IMPRINT",EDGE,{"disambiguationData":[TD([[subQ2,-1.0]])],"derivedFrom":subQ1}),1.0]])]});}
            var Q8;
            {var subQ0=sQuery(id+"F17.wireOp",EDGE,"E50.0.14.0");var subQ1=sQuery(id+"F17.wireOp",EDGE,"E42.right");var subQ2=makeQuery(id+"F17.imprint","INTERSECT",VERTEX,{"derivedFrom":[subQ1,subQ0]});Q8=makeQuery(id+"F17.imprint","IMPRINT",FACE,{"disambiguationData":[TD([[makeQuery(id+"F17.imprint","IMPRINT",EDGE,{"disambiguationData":[TD([[subQ2,-1.0]])],"derivedFrom":subQ1}),1.0]])]});}
            var Q9;
            {var subQ0=sQuery(id+"F17.wireOp",EDGE,"E50.0.16.0");var subQ1=sQuery(id+"F17.wireOp",EDGE,"E42.right");var subQ2=makeQuery(id+"F17.imprint","INTERSECT",VERTEX,{"derivedFrom":[subQ1,subQ0]});Q9=makeQuery(id+"F17.imprint","IMPRINT",FACE,{"disambiguationData":[TD([[makeQuery(id+"F17.imprint","IMPRINT",EDGE,{"disambiguationData":[TD([[subQ2,-1.0]])],"derivedFrom":subQ1}),1.0]])]});}
            var Q10;
            {var subQ3=sQuery(id+"F17.wireOp",EDGE,"E50.0.19.0");Q10=makeQuery(id+"F17.imprint","IMPRINT",FACE,{"disambiguationData":[TD([[makeQuery(id+"F17.imprint","IMPRINT",EDGE,{"derivedFrom":subQ3}),1.0]])]});}
            var Q11;
            {var subQ0=sQuery(id+"F17.wireOp",EDGE,"E47");var subQ1=sQuery(id+"F17.wireOp",EDGE,"E39.2");var subQ2=makeQuery(id+"F17.imprint","INTERSECT",VERTEX,{"derivedFrom":[subQ1,subQ0]});Q11=makeQuery(id+"F17.imprint","IMPRINT",FACE,{"disambiguationData":[TD([[makeQuery(id+"F17.imprint","IMPRINT",EDGE,{"disambiguationData":[TD([[subQ2,-1.0]])],"derivedFrom":subQ1}),-1.0]])]});}
            var Q12;
            {var subQ17=sQuery(id+"F17.wireOp",EDGE,"E85.0");Q12=makeQuery(id+"F17.imprint","IMPRINT",FACE,{"disambiguationData":[TD([[makeQuery(id+"F17.imprint","IMPRINT",EDGE,{"derivedFrom":subQ17}),1.0]])]});}
            var Q13;
            {var subQ0=sQuery(id+"F17.wireOp",EDGE,"E50.0.12.0");var subQ1=sQuery(id+"F17.wireOp",EDGE,"E42.right");var subQ2=makeQuery(id+"F17.imprint","INTERSECT",VERTEX,{"derivedFrom":[subQ1,subQ0]});Q13=makeQuery(id+"F17.imprint","IMPRINT",FACE,{"disambiguationData":[TD([[makeQuery(id+"F17.imprint","IMPRINT",EDGE,{"disambiguationData":[TD([[subQ2,-1.0]])],"derivedFrom":subQ1}),-1.0]])]});}
            var Q14;
            {var subQ0=sQuery(id+"F17.wireOp",EDGE,"E50.0.13.0");var subQ1=sQuery(id+"F17.wireOp",EDGE,"E42.right");var subQ2=makeQuery(id+"F17.imprint","INTERSECT",VERTEX,{"derivedFrom":[subQ1,subQ0]});Q14=makeQuery(id+"F17.imprint","IMPRINT",FACE,{"disambiguationData":[TD([[makeQuery(id+"F17.imprint","IMPRINT",EDGE,{"disambiguationData":[TD([[subQ2,-1.0]])],"derivedFrom":subQ1}),-1.0]])]});}
            var Q15;
            {var subQ0=sQuery(id+"F17.wireOp",EDGE,"E50.0.14.0");var subQ1=sQuery(id+"F17.wireOp",EDGE,"E42.right");var subQ2=makeQuery(id+"F17.imprint","INTERSECT",VERTEX,{"derivedFrom":[subQ1,subQ0]});Q15=makeQuery(id+"F17.imprint","IMPRINT",FACE,{"disambiguationData":[TD([[makeQuery(id+"F17.imprint","IMPRINT",EDGE,{"disambiguationData":[TD([[subQ2,-1.0]])],"derivedFrom":subQ1}),-1.0]])]});}
            var Q16;
            {var subQ0=sQuery(id+"F17.wireOp",EDGE,"E50.0.15.0");var subQ1=sQuery(id+"F17.wireOp",EDGE,"E42.right");var subQ2=makeQuery(id+"F17.imprint","INTERSECT",VERTEX,{"derivedFrom":[subQ1,subQ0]});Q16=makeQuery(id+"F17.imprint","IMPRINT",FACE,{"disambiguationData":[TD([[makeQuery(id+"F17.imprint","IMPRINT",EDGE,{"disambiguationData":[TD([[subQ2,-1.0]])],"derivedFrom":subQ1}),-1.0]])]});}
            var Q17;
            {var subQ0=sQuery(id+"F17.wireOp",EDGE,"E50.0.16.0");var subQ1=sQuery(id+"F17.wireOp",EDGE,"E42.right");var subQ2=makeQuery(id+"F17.imprint","INTERSECT",VERTEX,{"derivedFrom":[subQ1,subQ0]});Q17=makeQuery(id+"F17.imprint","IMPRINT",FACE,{"disambiguationData":[TD([[makeQuery(id+"F17.imprint","IMPRINT",EDGE,{"disambiguationData":[TD([[subQ2,-1.0]])],"derivedFrom":subQ1}),-1.0]])]});}
            var Q18;
            {var subQ10=sQuery(id+"F17.wireOp",EDGE,"E42.bottom");var subQ13=sQuery(id+"F17.wireOp",EDGE,"E43");var subQ21=makeQuery(id+"F17.imprint","INTERSECT",VERTEX,{"derivedFrom":[subQ10,subQ13]});Q18=makeQuery(id+"F17.imprint","IMPRINT",FACE,{"disambiguationData":[TD([[makeQuery(id+"F17.imprint","IMPRINT",EDGE,{"disambiguationData":[TD([[subQ21,-1.0]])],"derivedFrom":subQ10}),1.0]])]});}
            var Q19;
            {var subQ0=sQuery(id+"F17.wireOp",EDGE,"E45");var subQ6=sQuery(id+"F17.wireOp",EDGE,"E39.2");var subQ7=makeQuery(id+"F17.imprint","INTERSECT",VERTEX,{"derivedFrom":[subQ6,subQ0]});Q19=makeQuery(id+"F17.imprint","IMPRINT",FACE,{"disambiguationData":[TD([[makeQuery(id+"F17.imprint","IMPRINT",EDGE,{"disambiguationData":[TD([[subQ7,1.0]])],"derivedFrom":subQ6}),-1.0]])]});}
            var Q20;
            {var subQ3=sQuery(id+"F17.wireOp",EDGE,"E69.MirrorCS");var subQ9=sQuery(id+"F17.wireOp",EDGE,"E39.2");var subQ10=makeQuery(id+"F17.imprint","INTERSECT",VERTEX,{"derivedFrom":[subQ9,subQ3]});Q20=makeQuery(id+"F17.imprint","IMPRINT",FACE,{"disambiguationData":[TD([[makeQuery(id+"F17.imprint","IMPRINT",EDGE,{"disambiguationData":[TD([[subQ10,-1.0]])],"derivedFrom":subQ9}),-1.0]])]});}
            var Q21;
            {var subQ0=sQuery(id+"F17.wireOp",EDGE,"E67.MirrorCS");var subQ1=sQuery(id+"F17.wireOp",EDGE,"E39.2");var subQ2=makeQuery(id+"F17.imprint","INTERSECT",VERTEX,{"derivedFrom":[subQ1,subQ0]});Q21=makeQuery(id+"F17.imprint","IMPRINT",FACE,{"disambiguationData":[TD([[makeQuery(id+"F17.imprint","IMPRINT",EDGE,{"disambiguationData":[TD([[subQ2,-1.0]])],"derivedFrom":subQ1}),-1.0]])]});}
            var Q22;
            {var subQ0=sQuery(id+"F17.wireOp",EDGE,"E64.MirrorCS");Q22=makeQuery(id+"F17.imprint","IMPRINT",FACE,{"disambiguationData":[TD([[makeQuery(id+"F17.imprint","IMPRINT",EDGE,{"derivedFrom":subQ0}),1.0]])]});}
            var Q23;
            {var subQ0=sQuery(id+"F17.wireOp",EDGE,"E62.MirrorCS");Q23=makeQuery(id+"F17.imprint","IMPRINT",FACE,{"disambiguationData":[TD([[makeQuery(id+"F17.imprint","IMPRINT",EDGE,{"derivedFrom":subQ0}),1.0]])]});}
            var Q24;
            {var subQ6=sQuery(id+"F17.wireOp",EDGE,"E60.MirrorCS");Q24=makeQuery(id+"F17.imprint","IMPRINT",FACE,{"disambiguationData":[TD([[makeQuery(id+"F17.imprint","IMPRINT",EDGE,{"derivedFrom":subQ6}),1.0]])]});}
            var Q25;
            {var subQ0=sQuery(id+"F17.wireOp",EDGE,"E58.MirrorCS");Q25=makeQuery(id+"F17.imprint","IMPRINT",FACE,{"disambiguationData":[TD([[makeQuery(id+"F17.imprint","IMPRINT",EDGE,{"derivedFrom":subQ0}),1.0]])]});}
            var Q26;
            {var subQ0=sQuery(id+"F17.wireOp",EDGE,"E56.MirrorCS");Q26=makeQuery(id+"F17.imprint","IMPRINT",FACE,{"disambiguationData":[TD([[makeQuery(id+"F17.imprint","IMPRINT",EDGE,{"derivedFrom":subQ0}),1.0]])]});}
            var Q27;
            {var subQ0=sQuery(id+"F17.wireOp",EDGE,"E54.MirrorCS");Q27=makeQuery(id+"F17.imprint","IMPRINT",FACE,{"disambiguationData":[TD([[makeQuery(id+"F17.imprint","IMPRINT",EDGE,{"derivedFrom":subQ0}),1.0]])]});}
            var Q28;
            {var subQ0=sQuery(id+"F17.wireOp",EDGE,"E52.MirrorCS");Q28=makeQuery(id+"F17.imprint","IMPRINT",FACE,{"disambiguationData":[TD([[makeQuery(id+"F17.imprint","IMPRINT",EDGE,{"derivedFrom":subQ0}),1.0]])]});}
            var Q29;
            {var subQ0=sQuery(id+"F17.wireOp",EDGE,"E51.MirrorCS");Q29=makeQuery(id+"F17.imprint","IMPRINT",FACE,{"disambiguationData":[TD([[makeQuery(id+"F17.imprint","IMPRINT",EDGE,{"derivedFrom":subQ0}),-1.0]])]});}
            var Q30;
            {var subQ0=sQuery(id+"F17.wireOp",EDGE,"E108.MirrorCS");Q30=makeQuery(id+"F17.imprint","IMPRINT",FACE,{"disambiguationData":[TD([[makeQuery(id+"F17.imprint","IMPRINT",EDGE,{"derivedFrom":subQ0}),1.0]])]});}
            var Q31;
            {var subQ0=sQuery(id+"F17.wireOp",EDGE,"E113.MirrorCS");Q31=makeQuery(id+"F17.imprint","IMPRINT",FACE,{"disambiguationData":[TD([[makeQuery(id+"F17.imprint","IMPRINT",EDGE,{"derivedFrom":subQ0}),-1.0]])]});}
            var Q32;
            {var subQ0=sQuery(id+"F17.wireOp",EDGE,"E109.MirrorCS");Q32=makeQuery(id+"F17.imprint","IMPRINT",FACE,{"disambiguationData":[TD([[makeQuery(id+"F17.imprint","IMPRINT",EDGE,{"derivedFrom":subQ0}),-1.0]])]});}
            var Q33;
            {var subQ0=sQuery(id+"F17.wireOp",EDGE,"E115.MirrorCS");Q33=makeQuery(id+"F17.imprint","IMPRINT",FACE,{"disambiguationData":[TD([[makeQuery(id+"F17.imprint","IMPRINT",EDGE,{"derivedFrom":subQ0}),-1.0]])]});}
            var Q34;
            {var subQ0=sQuery(id+"F17.wireOp",EDGE,"E112.MirrorCS");Q34=makeQuery(id+"F17.imprint","IMPRINT",FACE,{"disambiguationData":[TD([[makeQuery(id+"F17.imprint","IMPRINT",EDGE,{"derivedFrom":subQ0}),-1.0]])]});}
            var Q35;
            {var subQ1=sQuery(id+"F17.wireOp",EDGE,"E103.MirrorCS");Q35=makeQuery(id+"F17.imprint","IMPRINT",FACE,{"disambiguationData":[TD([[makeQuery(id+"F17.imprint","IMPRINT",EDGE,{"derivedFrom":subQ1}),-1.0]])]});}
            var Q36;
            {var subQ0=sQuery(id+"F17.wireOp",EDGE,"E101.MirrorCS");var subQ1=sQuery(id+"F17.wireOp",EDGE,"E48");var subQ2=makeQuery(id+"F17.imprint","INTERSECT",VERTEX,{"derivedFrom":[subQ1,subQ0]});Q36=makeQuery(id+"F17.imprint","IMPRINT",FACE,{"disambiguationData":[TD([[makeQuery(id+"F17.imprint","IMPRINT",EDGE,{"disambiguationData":[TD([[subQ2,-1.0]])],"derivedFrom":subQ1}),1.0]])]});}
            var Q37;
            {var subQ0=sQuery(id+"F17.wireOp",EDGE,"E98.MirrorCS");var subQ1=sQuery(id+"F17.wireOp",EDGE,"E48");var subQ2=makeQuery(id+"F17.imprint","INTERSECT",VERTEX,{"derivedFrom":[subQ1,subQ0]});Q37=makeQuery(id+"F17.imprint","IMPRINT",FACE,{"disambiguationData":[TD([[makeQuery(id+"F17.imprint","IMPRINT",EDGE,{"disambiguationData":[TD([[subQ2,1.0]])],"derivedFrom":subQ1}),1.0]])]});}
            var Q38;
            {var subQ0=sQuery(id+"F17.wireOp",EDGE,"E100.MirrorCS");var subQ1=sQuery(id+"F17.wireOp",EDGE,"E48");var subQ2=makeQuery(id+"F17.imprint","INTERSECT",VERTEX,{"derivedFrom":[subQ1,subQ0]});Q38=makeQuery(id+"F17.imprint","IMPRINT",FACE,{"disambiguationData":[TD([[makeQuery(id+"F17.imprint","IMPRINT",EDGE,{"disambiguationData":[TD([[subQ2,-1.0]])],"derivedFrom":subQ1}),1.0]])]});}
            var Q39;
            {var subQ5=sQuery(id+"F17.wireOp",EDGE,"E105.MirrorCS");Q39=makeQuery(id+"F17.imprint","IMPRINT",FACE,{"disambiguationData":[TD([[makeQuery(id+"F17.imprint","IMPRINT",EDGE,{"derivedFrom":subQ5}),-1.0]])]});}
            var Q40;
            {var subQ0=sQuery(id+"F17.wireOp",EDGE,"E48");var subQ1=sQuery(id+"F17.wireOp",EDGE,"E39.2");var subQ2=makeQuery(id+"F17.imprint","INTERSECT",VERTEX,{"derivedFrom":[subQ1,subQ0]});Q40=makeQuery(id+"F17.imprint","IMPRINT",FACE,{"disambiguationData":[TD([[makeQuery(id+"F17.imprint","IMPRINT",EDGE,{"disambiguationData":[TD([[subQ2,1.0]])],"derivedFrom":subQ1}),-1.0]])]});}
            var Q41;
            {var subQ0=sQuery(id+"F17.wireOp",EDGE,"E120.MirrorCS");var subQ1=sQuery(id+"F17.wireOp",EDGE,"E98.MirrorCS");var subQ2=makeQuery(id+"F17.imprint","INTERSECT",VERTEX,{"derivedFrom":[subQ1,subQ0]});Q41=makeQuery(id+"F17.imprint","IMPRINT",FACE,{"disambiguationData":[TD([[makeQuery(id+"F17.imprint","IMPRINT",EDGE,{"disambiguationData":[TD([[subQ2,-1.0]])],"derivedFrom":subQ1}),1.0]])]});}
            var Q42;
            {var subQ0=sQuery(id+"F17.wireOp",EDGE,"E120.MirrorCS");var subQ1=sQuery(id+"F17.wireOp",EDGE,"E100.MirrorCS");var subQ2=makeQuery(id+"F17.imprint","INTERSECT",VERTEX,{"derivedFrom":[subQ1,subQ0]});Q42=makeQuery(id+"F17.imprint","IMPRINT",FACE,{"disambiguationData":[TD([[makeQuery(id+"F17.imprint","IMPRINT",EDGE,{"disambiguationData":[TD([[subQ2,-1.0]])],"derivedFrom":subQ1}),1.0]])]});}
            var Q43;
            Q43=makeQuery(id+"F17.imprint","IMPRINT",FACE,{"disambiguationData":[TD([[makeQuery(id+"F17.imprint","IMPRINT",EDGE,{"derivedFrom":sQuery(id+"F17.wireOp",EDGE,"E121.MirrorCS")}),1.0]])]});
            var Q44;
            {var subQ0=sQuery(id+"F17.wireOp",EDGE,"E120.MirrorCS");var subQ1=sQuery(id+"F17.wireOp",EDGE,"E98.MirrorCS");var subQ2=makeQuery(id+"F17.imprint","INTERSECT",VERTEX,{"derivedFrom":[subQ1,subQ0]});Q44=makeQuery(id+"F17.imprint","IMPRINT",FACE,{"disambiguationData":[TD([[makeQuery(id+"F17.imprint","IMPRINT",EDGE,{"disambiguationData":[TD([[subQ2,-1.0]])],"derivedFrom":subQ1}),-1.0]])]});}
            var Q45;
            {var subQ0=sQuery(id+"F17.wireOp",EDGE,"E120.MirrorCS");var subQ1=sQuery(id+"F17.wireOp",EDGE,"E99.MirrorCS");var subQ2=makeQuery(id+"F17.imprint","INTERSECT",VERTEX,{"derivedFrom":[subQ1,subQ0]});Q45=makeQuery(id+"F17.imprint","IMPRINT",FACE,{"disambiguationData":[TD([[makeQuery(id+"F17.imprint","IMPRINT",EDGE,{"disambiguationData":[TD([[subQ2,-1.0]])],"derivedFrom":subQ1}),-1.0]])]});}
            var Q46;
            {var subQ0=sQuery(id+"F17.wireOp",EDGE,"E120.MirrorCS");var subQ1=sQuery(id+"F17.wireOp",EDGE,"E101.MirrorCS");var subQ2=makeQuery(id+"F17.imprint","INTERSECT",VERTEX,{"derivedFrom":[subQ1,subQ0]});Q46=makeQuery(id+"F17.imprint","IMPRINT",FACE,{"disambiguationData":[TD([[makeQuery(id+"F17.imprint","IMPRINT",EDGE,{"disambiguationData":[TD([[subQ2,-1.0]])],"derivedFrom":subQ1}),1.0]])]});}
            var Q47;
            {var subQ6=sQuery(id+"F17.wireOp",EDGE,"E127.MirrorCS");Q47=makeQuery(id+"F17.imprint","IMPRINT",FACE,{"disambiguationData":[TD([[makeQuery(id+"F17.imprint","IMPRINT",EDGE,{"derivedFrom":subQ6}),-1.0]])]});}
            var Q48;
            {var subQ8=sQuery(id+"F17.wireOp",EDGE,"E122.MirrorCS");var subQ10=sQuery(id+"F17.wireOp",EDGE,"E160.MirrorCS");var subQ21=makeQuery(id+"F17.imprint","INTERSECT",VERTEX,{"derivedFrom":[subQ8,subQ10]});Q48=makeQuery(id+"F17.imprint","IMPRINT",FACE,{"disambiguationData":[TD([[makeQuery(id+"F17.imprint","IMPRINT",EDGE,{"disambiguationData":[TD([[subQ21,-1.0]])],"derivedFrom":subQ8}),-1.0]])]});}
            var Q49;
            {var subQ0=sQuery(id+"F17.wireOp",EDGE,"E142.MirrorCS");Q49=makeQuery(id+"F17.imprint","IMPRINT",FACE,{"disambiguationData":[TD([[makeQuery(id+"F17.imprint","IMPRINT",EDGE,{"derivedFrom":subQ0}),-1.0]])]});}
            var Q50;
            {var subQ0=sQuery(id+"F17.wireOp",EDGE,"E141.MirrorCS");Q50=makeQuery(id+"F17.imprint","IMPRINT",FACE,{"disambiguationData":[TD([[makeQuery(id+"F17.imprint","IMPRINT",EDGE,{"derivedFrom":subQ0}),-1.0]])]});}
            var Q51;
            {var subQ0=sQuery(id+"F17.wireOp",EDGE,"E140.MirrorCS");Q51=makeQuery(id+"F17.imprint","IMPRINT",FACE,{"disambiguationData":[TD([[makeQuery(id+"F17.imprint","IMPRINT",EDGE,{"derivedFrom":subQ0}),1.0]])]});}
            var Q52;
            {var subQ0=sQuery(id+"F17.wireOp",EDGE,"E137.MirrorCS");Q52=makeQuery(id+"F17.imprint","IMPRINT",FACE,{"disambiguationData":[TD([[makeQuery(id+"F17.imprint","IMPRINT",EDGE,{"derivedFrom":subQ0}),-1.0]])]});}
            var Q53;
            {var subQ0=sQuery(id+"F17.wireOp",EDGE,"E128.MirrorCS");Q53=makeQuery(id+"F17.imprint","IMPRINT",FACE,{"disambiguationData":[TD([[makeQuery(id+"F17.imprint","IMPRINT",EDGE,{"derivedFrom":subQ0}),-1.0]])]});}
            var Q54;
            {var subQ3=sQuery(id+"F17.wireOp",EDGE,"E131.MirrorCS");Q54=makeQuery(id+"F17.imprint","IMPRINT",FACE,{"disambiguationData":[TD([[makeQuery(id+"F17.imprint","IMPRINT",EDGE,{"derivedFrom":subQ3}),1.0]])]});}
            var Q55;
            {var subQ0=sQuery(id+"F17.wireOp",EDGE,"E133.MirrorCS");Q55=makeQuery(id+"F17.imprint","IMPRINT",FACE,{"disambiguationData":[TD([[makeQuery(id+"F17.imprint","IMPRINT",EDGE,{"derivedFrom":subQ0}),-1.0]])]});}
            var Q56;
            {var subQ0=sQuery(id+"F17.wireOp",EDGE,"E145.MirrorCS");Q56=makeQuery(id+"F17.imprint","IMPRINT",FACE,{"disambiguationData":[TD([[makeQuery(id+"F17.imprint","IMPRINT",EDGE,{"derivedFrom":subQ0}),-1.0]])]});}
            var Q57;
            {var subQ0=sQuery(id+"F17.wireOp",EDGE,"E134.MirrorCS");var subQ1=sQuery(id+"F17.wireOp",EDGE,"E39.2");var subQ2=makeQuery(id+"F17.imprint","INTERSECT",VERTEX,{"derivedFrom":[subQ1,subQ0]});Q57=makeQuery(id+"F17.imprint","IMPRINT",FACE,{"disambiguationData":[TD([[makeQuery(id+"F17.imprint","IMPRINT",EDGE,{"disambiguationData":[TD([[subQ2,-1.0]])],"derivedFrom":subQ1}),-1.0]])]});}
            var Q58;
            {var subQ3=sQuery(id+"F17.wireOp",EDGE,"E123.MirrorCS");var subQ5=sQuery(id+"F17.wireOp",EDGE,"E39.2");var subQ6=makeQuery(id+"F17.imprint","INTERSECT",VERTEX,{"derivedFrom":[subQ5,subQ3]});Q58=makeQuery(id+"F17.imprint","IMPRINT",FACE,{"disambiguationData":[TD([[makeQuery(id+"F17.imprint","IMPRINT",EDGE,{"disambiguationData":[TD([[subQ6,-1.0]])],"derivedFrom":subQ5}),-1.0]])]});}
            extrude(context, id + "F19", {"entities" : qUnion([Q0, Q1, Q2, Q3, Q4, Q5, Q6, Q7, Q8, Q9, Q10, Q11, Q12, Q13, Q14, Q15, Q16, Q17, Q18, Q19, Q20, Q21, Q22, Q23, Q24, Q25, Q26, Q27, Q28, Q29, Q30, Q31, Q32, Q33, Q34, Q35, Q36, Q37, Q38, Q39, Q40, Q41, Q42, Q43, Q44, Q45, Q46, Q47, Q48, Q49, Q50, Q51, Q52, Q53, Q54, Q55, Q56, Q57, Q58]), "operationType" : NewBodyOperationType.ADD, "oppositeDirection" : true, "depth" : 2 * mm, "offsetDistance" : 25 * mm});
        }
        {
            var Q0;
            Q0=makeQuery(id+"F8.boolean.opBoolean","COPY",FACE,{"derivedFrom":makeQuery(id+"F8.opExtrude","SWEPT_FACE",FACE,{"disambiguationData":[OSD([sQuery(id+"F7.wireOp",EDGE,"E14")])]})});
            var sketch = newSketch(context, id + "F20", { "sketchPlane" : qUnion([Q0])});
            skArc(sketch, "E163.0", {"start": v(-135, -157.5) * mm, "mid": v(0, -180.97) * mm, "end": v(135, -157.5) * mm});
            skLineSegment(sketch, "E164", {"start": v(-135, -157.5) * mm, "end": v(-135, -137.5) * mm});
            skLineSegment(sketch, "E165", {"start": v(-135, -137.5) * mm, "end": v(135, -137.5) * mm});
            skLineSegment(sketch, "E166", {"start": v(135, -137.5) * mm, "end": v(135, -157.5) * mm});
            skSolve(sketch);
        }
        {
            var Q0;
            Q0=qSketchRegion(id+"F20",true);
            var Q1;
            Q1=makeQuery(id+"F8.boolean.opBoolean","COPY",FACE,{"derivedFrom":makeQuery(id+"F8.opExtrude","SWEPT_FACE",FACE,{"disambiguationData":[OSD([sQuery(id+"F7.wireOp",EDGE,"E13")])]})});
            extrude(context, id + "F21", {"entities" : qUnion([Q0]), "endBound" : BoundingType.UP_TO_SURFACE, "depth" : 25 * mm, "endBoundEntityFace" : qUnion([Q1]), "offsetDistance" : 25 * mm});
        }
        {
            var Q0;
            Q0=makeQuery(id+"F6.boolean.opBoolean","COPY",FACE,{"derivedFrom":makeQuery(id+"F6.opExtrude","CAP_FACE",FACE,{"disambiguationData":[OSD([sQuery(id+"F5.wireOp",EDGE,"E7.0.2"),sQuery(id+"F5.wireOp",EDGE,"E8"),sQuery(id+"F5.wireOp",EDGE,"E9"),sQuery(id+"F5.wireOp",EDGE,"E10.MirrorCS"),sQuery(id+"F5.wireOp",EDGE,"E11.MirrorCS")])],"isStart":true})});
            cPlane(context, id + "F22", {"entities" : qUnion([Q0]), "cplaneType" : CPlaneType.OFFSET, "offset" : 230 * mm, "width" : 150 * mm, "height" : 150 * mm});
        }
        {
            var Q0;
            Q0=qCreatedBy(id+"F22.planeOp",FACE);
            var sketch = newSketch(context, id + "F23", { "sketchPlane" : qUnion([Q0])});
            skLineSegment(sketch, "E167", {"start": v(0, 33.17) * mm, "end": v(0, -218.1) * mm, "construction": true});
            skLineSegment(sketch, "E168", {"start": v(-50, 0) * mm, "end": v(-50, -209.98) * mm, "construction": true});
            skLineSegment(sketch, "E169.0.0", {"start": v(-90, -129.3) * mm, "end": v(90, -129.3) * mm});
            skLineSegment(sketch, "E169.0.2", {"start": v(90, -129.3) * mm, "end": v(-90, -129.3) * mm});
            skLineSegment(sketch, "E170", {"start": v(-60, -129.3) * mm, "end": v(-56, -163.8) * mm});
            skLineSegment(sketch, "E171", {"start": v(-60.9, -163.8) * mm, "end": v(-38.9, -163.8) * mm});
            skLineSegment(sketch, "E172", {"start": v(-50, -163.8) * mm, "end": v(-50, -129.3) * mm});
            skSolve(sketch);
        }
        {
            var Q0;
            {var subQ0=sQuery(id+"F23.wireOp",EDGE,"E170");Q0=makeQuery(id+"F23.imprint","IMPRINT",FACE,{"disambiguationData":[TD([[makeQuery(id+"F23.imprint","IMPRINT",EDGE,{"derivedFrom":subQ0}),1.0]])]});}
            var Q1;
            Q1=sQuery(id+"F23.wireOp",EDGE,"E172");
            revolve(context, id + "F24", {"surfaceOperationType" : NewSurfaceOperationType.NEW, "entities" : qUnion([Q0]), "axis" : qUnion([Q1]), "revolveType" : RevolveType.FULL});
        }
        {
            var Q0;
            Q0=makeQuery(id+"F24.opRevolve","SWEPT_FACE",FACE,{"disambiguationData":[OSD([sQuery(id+"F23.wireOp",EDGE,"E171")])]});
            var sketch = newSketch(context, id + "F25", { "sketchPlane" : qUnion([Q0])});
            skCircle(sketch, "E173.0", {"center": v(-50, 680) * mm, "radius": 6 * mm, "construction": true});
            skLineSegment(sketch, "E174", {"start": v(-50, 717.97) * mm, "end": v(-50, 638.06) * mm, "construction": true});
            skLineSegment(sketch, "E175.bottom", {"start": v(-60, 695) * mm, "end": v(-40, 695) * mm});
            skLineSegment(sketch, "E175.top", {"start": v(-57, 665) * mm, "end": v(-57, 665) * mm});
            skLineSegment(sketch, "E175.left", {"start": v(-60, 695) * mm, "end": v(-60, 668) * mm});
            skLineSegment(sketch, "E176.top", {"start": v(-54, 655) * mm, "end": v(-46, 655) * mm});
            skLineSegment(sketch, "E176.left", {"start": v(-54, 662) * mm, "end": v(-54, 655) * mm});
            skPoint(sketch, "E177.visualSharp", {"position": v(-60, 665) * mm});
            skArc(sketch, "E177.filletArc", {"start": v(-60, 668) * mm, "mid": v(-59.12, 665.88) * mm, "end": v(-57, 665) * mm});
            skArc(sketch, "E178.filletArc", {"start": v(-54, 662) * mm, "mid": v(-54.88, 664.12) * mm, "end": v(-57, 665) * mm});
            skLineSegment(sketch, "E179", {"start": v(-57, 665) * mm, "end": v(-50, 665) * mm});
            skLineSegment(sketch, "E180", {"start": v(-50, 695) * mm, "end": v(-50, 655) * mm});
            skSolve(sketch);
        }
        {
            var Q0;
            {var subQ1=sQuery(id+"F25.wireOp",EDGE,"E175.left");Q0=makeQuery(id+"F25.imprint","IMPRINT",FACE,{"disambiguationData":[TD([[makeQuery(id+"F25.imprint","IMPRINT",EDGE,{"derivedFrom":subQ1}),1.0]])]});}
            var Q1;
            {var subQ0=sQuery(id+"F25.wireOp",EDGE,"E180");var subQ1=makeQuery(id+"F24.opRevolve","SWEPT_EDGE",EDGE,{"disambiguationData":[OSD([sQuery(id+"F23.wireOp",EDGE,"E170"),sQuery(id+"F23.wireOp",EDGE,"E171")])]});var subQ2=makeQuery(id+"F25.imprint","INTERSECT",VERTEX,{"disambiguationData":[OD(0.0)],"derivedFrom":[subQ1,subQ0]});Q1=makeQuery(id+"F25.imprint","IMPRINT",FACE,{"disambiguationData":[TD([[makeQuery(id+"F25.imprint","IMPRINT",EDGE,{"disambiguationData":[TD([[subQ2,-1.0]])],"derivedFrom":subQ0}),-1.0]])]});}
            var Q2;
            {var subQ1=sQuery(id+"F25.wireOp",EDGE,"E176.left");Q2=makeQuery(id+"F25.imprint","IMPRINT",FACE,{"disambiguationData":[TD([[makeQuery(id+"F25.imprint","IMPRINT",EDGE,{"derivedFrom":subQ1}),1.0]])]});}
            var Q3;
            Q3=sQuery(id+"F25.wireOp",EDGE,"E174");
            revolve(context, id + "F26", {"operationType" : NewBodyOperationType.ADD, "surfaceOperationType" : NewSurfaceOperationType.NEW, "entities" : qUnion([Q0, Q1, Q2]), "axis" : qUnion([Q3]), "revolveType" : RevolveType.FULL});
        }
        {
            var Q0;
            Q0=sQuery(id+"F25.wireOp",VERTEX,"E175.left.start");
            var Q1;
            Q1=sQuery(id+"F25.wireOp",VERTEX,"E177.filletArc.start");
            var Q2;
            Q2=sQuery(id+"F25.wireOp",VERTEX,"E173.0.center");
            cPlane(context, id + "F27", {"entities" : qUnion([Q0, Q1, Q2]), "cplaneType" : CPlaneType.THREE_POINT, "offset" : 25 * mm, "width" : 150 * mm, "height" : 150 * mm});
        }
        {
            var Q0;
            Q0=qCreatedBy(id+"F27.planeOp",FACE);
            var sketch = newSketch(context, id + "F28", { "sketchPlane" : qUnion([Q0])});
            skLineSegment(sketch, "E181.0", {"start": v(40, 695) * mm, "end": v(60, 695) * mm});
            skLineSegment(sketch, "E182", {"start": v(50, 714.18) * mm, "end": v(50, 675.84) * mm, "construction": true});
            skPoint(sketch, "E182.startSnap0", {"position": v(50, 695) * mm});
            skLineSegment(sketch, "E183", {"start": v(48, 695) * mm, "end": v(48, 700) * mm});
            skLineSegment(sketch, "E184", {"start": v(48, 700) * mm, "end": v(42.5, 700) * mm});
            skLineSegment(sketch, "E185", {"start": v(42.5, 700) * mm, "end": v(42.5, 715) * mm});
            skLineSegment(sketch, "E186", {"start": v(42.5, 715) * mm, "end": v(57.5, 715) * mm});
            skLineSegment(sketch, "E187", {"start": v(57.5, 715) * mm, "end": v(57.5, 700) * mm});
            skLineSegment(sketch, "E188", {"start": v(57.5, 700) * mm, "end": v(52, 700) * mm});
            skLineSegment(sketch, "E189", {"start": v(52, 700) * mm, "end": v(52, 695) * mm});
            skLineSegment(sketch, "E190.bottom", {"start": v(44.5, 713) * mm, "end": v(55.5, 713) * mm});
            skLineSegment(sketch, "E190.top", {"start": v(44.5, 702) * mm, "end": v(55.5, 702) * mm});
            skLineSegment(sketch, "E190.left", {"start": v(44.5, 713) * mm, "end": v(44.5, 702) * mm});
            skLineSegment(sketch, "E190.right", {"start": v(55.5, 713) * mm, "end": v(55.5, 702) * mm});
            skSolve(sketch);
        }
        {
            var Q0;
            {var subQ1=sQuery(id+"F28.wireOp",EDGE,"E183");Q0=makeQuery(id+"F28.imprint","IMPRINT",FACE,{"disambiguationData":[TD([[makeQuery(id+"F28.imprint","IMPRINT",EDGE,{"derivedFrom":subQ1}),-1.0]])]});}
            extrude(context, id + "F29", {"entities" : qUnion([Q0]), "operationType" : NewBodyOperationType.ADD, "depth" : 5 * mm, "offsetDistance" : 25 * mm, "symmetric" : true});
        }
        {
            var Q0;
            Q0=makeQuery(id+"F29.opExtrude","SWEPT_EDGE",EDGE,{"disambiguationData":[OSD([sQuery(id+"F28.wireOp",EDGE,"E186"),sQuery(id+"F28.wireOp",EDGE,"E187")])]});
            var Q1;
            Q1=makeQuery(id+"F29.opExtrude","SWEPT_EDGE",EDGE,{"disambiguationData":[OSD([sQuery(id+"F28.wireOp",EDGE,"E187"),sQuery(id+"F28.wireOp",EDGE,"E188")])]});
            var Q2;
            Q2=makeQuery(id+"F29.opExtrude","SWEPT_EDGE",EDGE,{"disambiguationData":[OSD([sQuery(id+"F28.wireOp",EDGE,"E185"),sQuery(id+"F28.wireOp",EDGE,"E186")])]});
            var Q3;
            Q3=makeQuery(id+"F29.opExtrude","SWEPT_EDGE",EDGE,{"disambiguationData":[OSD([sQuery(id+"F28.wireOp",EDGE,"E184"),sQuery(id+"F28.wireOp",EDGE,"E185")])]});
            fillet(context, id + "F30", {"entities" : qUnion([Q0, Q1, Q2, Q3]), "radius" : 3 * mm, "tangentPropagation" : true, "allowEdgeOverflow" : false});
        }
        {
            var Q0;
            Q0=makeQuery(id+"F29.opExtrude","SWEPT_EDGE",EDGE,{"disambiguationData":[OSD([sQuery(id+"F28.wireOp",EDGE,"E190.bottom"),sQuery(id+"F28.wireOp",EDGE,"E190.right")])]});
            var Q1;
            Q1=makeQuery(id+"F29.opExtrude","SWEPT_EDGE",EDGE,{"disambiguationData":[OSD([sQuery(id+"F28.wireOp",EDGE,"E190.bottom"),sQuery(id+"F28.wireOp",EDGE,"E190.left")])]});
            var Q2;
            Q2=makeQuery(id+"F29.opExtrude","SWEPT_EDGE",EDGE,{"disambiguationData":[OSD([sQuery(id+"F28.wireOp",EDGE,"E190.top"),sQuery(id+"F28.wireOp",EDGE,"E190.left")])]});
            var Q3;
            Q3=makeQuery(id+"F29.opExtrude","SWEPT_EDGE",EDGE,{"disambiguationData":[OSD([sQuery(id+"F28.wireOp",EDGE,"E190.top"),sQuery(id+"F28.wireOp",EDGE,"E190.right")])]});
            fillet(context, id + "F31", {"entities" : qUnion([Q0, Q1, Q2, Q3]), "radius" : 1 * mm, "tangentPropagation" : true, "allowEdgeOverflow" : false});
        }
        {
            var Q0;
            Q0=makeQuery(id+"F24.opRevolve","SWEPT_BODY",BODY,{"disambiguationData":[OSD([sQuery(id+"F23.wireOp",EDGE,"E169.0.2"),sQuery(id+"F23.wireOp",EDGE,"E170"),sQuery(id+"F23.wireOp",EDGE,"E171"),sQuery(id+"F23.wireOp",EDGE,"E172")])]});
            var Q1;
            Q1=qCreatedBy(makeId("Right.planeOp"),FACE);
            mirror(context, id + "F32", {"entities" : qUnion([Q0]), "mirrorPlane" : qUnion([Q1])});
        }
        {
            var Q0;
            Q0=qCreatedBy(makeId("Right.planeOp"),FACE);
            cPlane(context, id + "F33", {"entities" : qUnion([Q0]), "cplaneType" : CPlaneType.OFFSET, "offset" : (315 / 2 - 50) * mm, "width" : 150 * mm, "height" : 150 * mm});
        }
        {
            var Q0;
            Q0=qCreatedBy(id+"F33.planeOp",FACE);
            var sketch = newSketch(context, id + "F34", { "sketchPlane" : qUnion([Q0])});
            skLineSegment(sketch, "E191.0", {"start": v(157.5, 955) * mm, "end": v(157.5, 0) * mm});
            skLineSegment(sketch, "E192", {"start": v(157.5, 920) * mm, "end": v(166.5, 920) * mm});
            skLineSegment(sketch, "E193", {"start": v(166.5, 920) * mm, "end": v(157.5, 904.41) * mm});
            skLineSegment(sketch, "E194", {"start": v(157.5, 904.41) * mm, "end": v(157.5, 886.41) * mm});
            skLineSegment(sketch, "E195", {"start": v(157.5, 886.41) * mm, "end": v(149.5, 886.41) * mm});
            skLineSegment(sketch, "E196", {"start": v(149.5, 886.41) * mm, "end": v(149.5, 920) * mm});
            skLineSegment(sketch, "E197", {"start": v(149.5, 920) * mm, "end": v(157.5, 920) * mm});
            skSolve(sketch);
        }
        {
            var Q0;
            {var subQ4=sQuery(id+"F34.wireOp",EDGE,"E192");var subQ6=sQuery(id+"F34.wireOp",EDGE,"E195");Q0=qUnion([makeQuery(id+"F34.imprint","IMPRINT",FACE,{"disambiguationData":[TD([[makeQuery(id+"F34.imprint","IMPRINT",EDGE,{"derivedFrom":subQ6}),-1.0]])]}),makeQuery(id+"F34.imprint","IMPRINT",FACE,{"disambiguationData":[TD([[makeQuery(id+"F34.imprint","IMPRINT",EDGE,{"derivedFrom":subQ4}),-1.0]])]})]);}
            extrude(context, id + "F35", {"entities" : qUnion([Q0]), "operationType" : NewBodyOperationType.REMOVE, "oppositeDirection" : true, "depth" : 10 * mm, "offsetDistance" : 25 * mm, "symmetric" : true});
        }
        {
            var Q0;
            Q0=qCreatedBy(id+"F33.planeOp",FACE);
            cPlane(context, id + "F36", {"entities" : qUnion([Q0]), "cplaneType" : CPlaneType.OFFSET, "offset" : 20 * mm, "oppositeDirection" : true, "width" : 150 * mm, "height" : 150 * mm});
        }
        {
            var Q0;
            Q0=qCreatedBy(id+"F36.planeOp",FACE);
            var sketch = newSketch(context, id + "F37", { "sketchPlane" : qUnion([Q0])});
            skLineSegment(sketch, "E198.0", {"start": v(157.5, 886.41) * mm, "end": v(149.5, 886.41) * mm});
            skLineSegment(sketch, "E198.1", {"start": v(149.5, 886.41) * mm, "end": v(149.5, 920) * mm});
            skLineSegment(sketch, "E198.2", {"start": v(149.5, 920) * mm, "end": v(157.5, 920) * mm});
            skLineSegment(sketch, "E198.3", {"start": v(157.5, 920) * mm, "end": v(166.5, 920) * mm});
            skLineSegment(sketch, "E198.4", {"start": v(166.5, 920) * mm, "end": v(157.5, 904.41) * mm});
            skLineSegment(sketch, "E198.5", {"start": v(157.5, 904.41) * mm, "end": v(157.5, 886.41) * mm});
            skSolve(sketch);
        }
        {
            var Q0;
            Q0=qSketchRegion(id+"F37",true);
            extrude(context, id + "F38", {"entities" : qUnion([Q0]), "operationType" : NewBodyOperationType.REMOVE, "oppositeDirection" : true, "depth" : 10 * mm, "offsetDistance" : 25 * mm, "symmetric" : true});
        }
        {
            var Q0;
            {var subQ4=sQuery(id+"F34.wireOp",EDGE,"E192");var subQ6=sQuery(id+"F34.wireOp",EDGE,"E195");Q0=qUnion([makeQuery(id+"F34.imprint","IMPRINT",FACE,{"disambiguationData":[TD([[makeQuery(id+"F34.imprint","IMPRINT",EDGE,{"derivedFrom":subQ6}),-1.0]])]}),makeQuery(id+"F34.imprint","IMPRINT",FACE,{"disambiguationData":[TD([[makeQuery(id+"F34.imprint","IMPRINT",EDGE,{"derivedFrom":subQ4}),-1.0]])]})]);}
            extrude(context, id + "F39", {"entities" : qUnion([Q0]), "depth" : 10 * mm, "offsetDistance" : 25 * mm, "symmetric" : true});
        }
        {
            var Q0;
            Q0=qSketchRegion(id+"F37",true);
            extrude(context, id + "F40", {"entities" : qUnion([Q0]), "depth" : 10 * mm, "offsetDistance" : 25 * mm, "symmetric" : true});
        }
        {
            var Q0;
            {var subQ0=sQuery(id+"F0.wireOp",EDGE,"E0.left");var subQ1=sQuery(id+"F0.wireOp",EDGE,"E0.bottom");Q0=makeQuery(id+"F13.opFillet","BLEND_VERTEX",VERTEX,{"blendedFrom":[makeQuery(id+"F1.opExtrude","CAP_VERTEX",VERTEX,{"disambiguationData":[OSD([subQ1,subQ0])],"isStart":false}),makeQuery(id+"F1.opExtrude","SWEPT_EDGE",EDGE,{"disambiguationData":[OSD([subQ1,subQ0])]}),makeQuery(id+"F1.opExtrude","CAP_EDGE",EDGE,{"disambiguationData":[OSD([subQ0])],"isStart":false}),makeQuery(id+"F1.opExtrude","SWEPT_FACE",FACE,{"disambiguationData":[OSD([subQ0])]})],"blendedInto":[makeQuery(id+"F1.opExtrude","SWEPT_FACE",FACE,{"disambiguationData":[OSD([subQ0])]})]});}
            var Q1;
            {var subQ0=sQuery(id+"F0.wireOp",EDGE,"E1");var subQ1=sQuery(id+"F0.wireOp",EDGE,"E0.top");var subQ2=sQuery(id+"F0.wireOp",EDGE,"E0.left");var subQ3=makeQuery(id+"F1.opExtrude","SWEPT_FACE",FACE,{"disambiguationData":[OSD([subQ2])]});var subQ4=sQuery(id+"F0.wireOp",EDGE,"E0.bottom");Q1=makeQuery(id+"F13.opFillet","BLEND_VERTEX",VERTEX,{"blendedFrom":[makeQuery(id+"F1.opExtrude","SWEPT_EDGE",EDGE,{"disambiguationData":[OSD([subQ4,subQ2])]}),subQ3,makeQuery(id+"F10.boolean.opBoolean","SPLIT",FACE,{"disambiguationData":[TD([subQ3])],"derivedFrom":makeQuery(id+"F1.opExtrude","CAP_FACE",FACE,{"disambiguationData":[OSD([subQ4,subQ1,subQ2,sQuery(id+"F0.wireOp",EDGE,"E0.right"),subQ0])],"isStart":true})})],"blendedInto":[subQ3,makeQuery(id+"F10.boolean.opBoolean","SPLIT",FACE,{"disambiguationData":[TD([subQ3])],"derivedFrom":makeQuery(id+"F1.opExtrude","CAP_FACE",FACE,{"disambiguationData":[OSD([subQ4,subQ1,subQ2,sQuery(id+"F0.wireOp",EDGE,"E0.right"),subQ0])],"isStart":true})})]});}
            var Q2;
            {var subQ0=sQuery(id+"F0.wireOp",EDGE,"E0.right");var subQ1=sQuery(id+"F0.wireOp",EDGE,"E0.bottom");Q2=makeQuery(id+"F13.opFillet","BLEND_VERTEX",VERTEX,{"blendedFrom":[makeQuery(id+"F1.opExtrude","CAP_VERTEX",VERTEX,{"disambiguationData":[OSD([subQ1,subQ0])],"isStart":false}),makeQuery(id+"F1.opExtrude","SWEPT_EDGE",EDGE,{"disambiguationData":[OSD([subQ1,subQ0])]}),makeQuery(id+"F1.opExtrude","CAP_EDGE",EDGE,{"disambiguationData":[OSD([subQ0])],"isStart":false}),makeQuery(id+"F1.opExtrude","SWEPT_FACE",FACE,{"disambiguationData":[OSD([subQ0])]})],"blendedInto":[makeQuery(id+"F1.opExtrude","SWEPT_FACE",FACE,{"disambiguationData":[OSD([subQ0])]})]});}
            cPlane(context, id + "F41", {"entities" : qUnion([Q0, Q1, Q2]), "cplaneType" : CPlaneType.THREE_POINT, "offset" : 25 * mm, "width" : 150 * mm, "height" : 150 * mm});
        }
        {
            var Q0;
            Q0=qCreatedBy(id+"F41.planeOp",FACE);
            var sketch = newSketch(context, id + "F42", { "sketchPlane" : qUnion([Q0])});
            skLineSegment(sketch, "E199.bottom", {"start": v(-125, 945) * mm, "end": v(125, 945) * mm});
            skLineSegment(sketch, "E199.top", {"start": v(-125, 855) * mm, "end": v(125, 855) * mm});
            skLineSegment(sketch, "E199.left", {"start": v(-125, 945) * mm, "end": v(-125, 855) * mm});
            skLineSegment(sketch, "E199.right", {"start": v(125, 945) * mm, "end": v(125, 855) * mm});
            skSolve(sketch);
        }
        {
            var Q0;
            Q0=qSketchRegion(id+"F42",true);
            extrude(context, id + "F43", {"entities" : qUnion([Q0]), "operationType" : NewBodyOperationType.REMOVE, "endBound" : BoundingType.THROUGH_ALL, "depth" : 25 * mm, "offsetDistance" : 25 * mm});
        }
        {
            var Q0;
            Q0=makeQuery(id+"F43.boolean.opBoolean","COPY",FACE,{"derivedFrom":makeQuery(id+"F43.opExtrude","CAP_FACE",FACE,{"disambiguationData":[OSD([sQuery(id+"F42.wireOp",EDGE,"E199.bottom"),sQuery(id+"F42.wireOp",EDGE,"E199.top"),sQuery(id+"F42.wireOp",EDGE,"E199.left"),sQuery(id+"F42.wireOp",EDGE,"E199.right")])],"isStart":true})});
            var sketch = newSketch(context, id + "F44", { "sketchPlane" : qUnion([Q0])});
            skLineSegment(sketch, "E200.bottom", {"start": v(-125, 945) * mm, "end": v(125, 945) * mm});
            skLineSegment(sketch, "E200.top", {"start": v(-125, 855) * mm, "end": v(125, 855) * mm});
            skLineSegment(sketch, "E200.left", {"start": v(-125, 945) * mm, "end": v(-125, 855) * mm});
            skLineSegment(sketch, "E200.right", {"start": v(125, 945) * mm, "end": v(125, 855) * mm});
            skLineSegment(sketch, "E201.bottom", {"start": v(75, 930) * mm, "end": v(85, 930) * mm});
            skLineSegment(sketch, "E201.top", {"start": v(75, 925) * mm, "end": v(85, 925) * mm});
            skLineSegment(sketch, "E201.left", {"start": v(75, 930) * mm, "end": v(75, 925) * mm});
            skLineSegment(sketch, "E201.right", {"start": v(85, 930) * mm, "end": v(85, 925) * mm});
            skLineSegment(sketch, "E202.bottom", {"start": v(75, 920) * mm, "end": v(85, 920) * mm});
            skLineSegment(sketch, "E202.top", {"start": v(75, 915) * mm, "end": v(85, 915) * mm});
            skLineSegment(sketch, "E202.left", {"start": v(75, 920) * mm, "end": v(75, 915) * mm});
            skLineSegment(sketch, "E202.right", {"start": v(85, 920) * mm, "end": v(85, 915) * mm});
            skSolve(sketch);
        }
        {
            var Q0;
            Q0=makeQuery(id+"F44.imprint","IMPRINT",FACE,{"disambiguationData":[TD([[makeQuery(id+"F44.imprint","IMPRINT",EDGE,{"derivedFrom":sQuery(id+"F44.wireOp",EDGE,"E200.bottom")}),-1.0]])]});
            var Q1;
            Q1=makeQuery(id+"F44.imprint","IMPRINT",FACE,{"disambiguationData":[TD([[makeQuery(id+"F44.imprint","IMPRINT",EDGE,{"derivedFrom":sQuery(id+"F44.wireOp",EDGE,"6fba481b-f54a-40dc-850f-529da61e2d5d.sketch_text.stroke-14")}),1.0]])]});
            var Q2;
            Q2=makeQuery(id+"F44.imprint","IMPRINT",FACE,{"disambiguationData":[TD([[makeQuery(id+"F44.imprint","IMPRINT",EDGE,{"derivedFrom":sQuery(id+"F44.wireOp",EDGE,"6fba481b-f54a-40dc-850f-529da61e2d5d.sketch_text.stroke-50")}),1.0]])]});
            var Q3;
            Q3=makeQuery(id+"F44.imprint","IMPRINT",FACE,{"disambiguationData":[TD([[makeQuery(id+"F44.imprint","IMPRINT",EDGE,{"derivedFrom":sQuery(id+"F44.wireOp",EDGE,"0e071c30-8112-48db-a0b7-94a150164aee.sketch_text.stroke-20")}),1.0]])]});
            var Q4;
            Q4=makeQuery(id+"F44.imprint","IMPRINT",FACE,{"disambiguationData":[TD([[makeQuery(id+"F44.imprint","IMPRINT",EDGE,{"derivedFrom":sQuery(id+"F44.wireOp",EDGE,"e2d7af9a-f6d1-4b82-89d6-a8a0b8d7c55a.sketch_text.stroke-23")}),1.0]])]});
            var Q5;
            Q5=makeQuery(id+"F44.imprint","IMPRINT",FACE,{"disambiguationData":[TD([[makeQuery(id+"F44.imprint","IMPRINT",EDGE,{"derivedFrom":sQuery(id+"F44.wireOp",EDGE,"e2d7af9a-f6d1-4b82-89d6-a8a0b8d7c55a.sketch_text.stroke-44")}),1.0]])]});
            var Q6;
            {var subQ0=sQuery(id+"F0.wireOp",EDGE,"E0.right");var subQ1=sQuery(id+"F0.wireOp",EDGE,"E0.bottom");var subQ2=sQuery(id+"F0.wireOp",EDGE,"E1");var subQ4=sQuery(id+"F0.wireOp",EDGE,"E0.left");Q6=makeQuery(id+"F6.boolean.opBoolean","SPLIT",FACE,{"disambiguationData":[TD([makeQuery(id+"F1.opExtrude","CAP_FACE",FACE,{"disambiguationData":[OSD([subQ1,sQuery(id+"F0.wireOp",EDGE,"E0.top"),subQ4,subQ0,subQ2])],"isStart":false})])],"derivedFrom":makeQuery(id+"F1.opExtrude","SWEPT_FACE",FACE,{"disambiguationData":[OSD([subQ2])]})});}
            extrude(context, id + "F45", {"entities" : qUnion([Q0, Q1, Q2, Q3, Q4, Q5]), "operationType" : NewBodyOperationType.ADD, "endBound" : BoundingType.UP_TO_SURFACE, "depth" : 25 * mm, "endBoundEntityFace" : qUnion([Q6]), "offsetDistance" : 25 * mm});
        }
        {
            var Q0;
            Q0=makeQuery(id+"F44.imprint","IMPRINT",FACE,{"disambiguationData":[TD([[makeQuery(id+"F44.imprint","IMPRINT",EDGE,{"derivedFrom":sQuery(id+"F44.wireOp",EDGE,"E201.bottom")}),-1.0]])]});
            var Q1;
            {var subQ0=sQuery(id+"F0.wireOp",EDGE,"E0.right");var subQ1=sQuery(id+"F0.wireOp",EDGE,"E0.bottom");var subQ2=sQuery(id+"F0.wireOp",EDGE,"E1");var subQ4=sQuery(id+"F0.wireOp",EDGE,"E0.left");Q1=makeQuery(id+"F45.boolean.opBoolean","MERGE",FACE,{"derivedFrom":[makeQuery(id+"F6.boolean.opBoolean","SPLIT",FACE,{"disambiguationData":[TD([makeQuery(id+"F1.opExtrude","CAP_FACE",FACE,{"disambiguationData":[OSD([subQ1,sQuery(id+"F0.wireOp",EDGE,"E0.top"),subQ4,subQ0,subQ2])],"isStart":false})])],"derivedFrom":makeQuery(id+"F1.opExtrude","SWEPT_FACE",FACE,{"disambiguationData":[OSD([subQ2])]})}),makeQuery(id+"F45.opExtrude","CAP_FACE",FACE,{"disambiguationData":[OSD([sQuery(id+"F44.wireOp",EDGE,"E200.bottom"),sQuery(id+"F44.wireOp",EDGE,"E200.top"),sQuery(id+"F44.wireOp",EDGE,"E200.left"),sQuery(id+"F44.wireOp",EDGE,"E200.right"),sQuery(id+"F44.wireOp",EDGE,"E201.bottom"),sQuery(id+"F44.wireOp",EDGE,"E201.top"),sQuery(id+"F44.wireOp",EDGE,"E201.left"),sQuery(id+"F44.wireOp",EDGE,"E201.right"),sQuery(id+"F44.wireOp",EDGE,"E202.bottom"),sQuery(id+"F44.wireOp",EDGE,"E202.top"),sQuery(id+"F44.wireOp",EDGE,"E202.left"),sQuery(id+"F44.wireOp",EDGE,"E202.right"),sQuery(id+"F44.wireOp",EDGE,"0e071c30-8112-48db-a0b7-94a150164aee.sketch_text.stroke-0"),sQuery(id+"F44.wireOp",EDGE,"0e071c30-8112-48db-a0b7-94a150164aee.sketch_text.stroke-1"),sQuery(id+"F44.wireOp",EDGE,"0e071c30-8112-48db-a0b7-94a150164aee.sketch_text.stroke-2"),sQuery(id+"F44.wireOp",EDGE,"0e071c30-8112-48db-a0b7-94a150164aee.sketch_text.stroke-3"),sQuery(id+"F44.wireOp",EDGE,"0e071c30-8112-48db-a0b7-94a150164aee.sketch_text.stroke-4"),sQuery(id+"F44.wireOp",EDGE,"0e071c30-8112-48db-a0b7-94a150164aee.sketch_text.stroke-5"),sQuery(id+"F44.wireOp",EDGE,"0e071c30-8112-48db-a0b7-94a150164aee.sketch_text.stroke-6"),sQuery(id+"F44.wireOp",EDGE,"0e071c30-8112-48db-a0b7-94a150164aee.sketch_text.stroke-7"),sQuery(id+"F44.wireOp",EDGE,"0e071c30-8112-48db-a0b7-94a150164aee.sketch_text.stroke-8"),sQuery(id+"F44.wireOp",EDGE,"0e071c30-8112-48db-a0b7-94a150164aee.sketch_text.stroke-9"),sQuery(id+"F44.wireOp",EDGE,"0e071c30-8112-48db-a0b7-94a150164aee.sketch_text.stroke-10"),sQuery(id+"F44.wireOp",EDGE,"0e071c30-8112-48db-a0b7-94a150164aee.sketch_text.stroke-11"),sQuery(id+"F44.wireOp",EDGE,"0e071c30-8112-48db-a0b7-94a150164aee.sketch_text.stroke-12"),sQuery(id+"F44.wireOp",EDGE,"0e071c30-8112-48db-a0b7-94a150164aee.sketch_text.stroke-13"),sQuery(id+"F44.wireOp",EDGE,"0e071c30-8112-48db-a0b7-94a150164aee.sketch_text.stroke-14"),sQuery(id+"F44.wireOp",EDGE,"0e071c30-8112-48db-a0b7-94a150164aee.sketch_text.stroke-15"),sQuery(id+"F44.wireOp",EDGE,"0e071c30-8112-48db-a0b7-94a150164aee.sketch_text.stroke-16"),sQuery(id+"F44.wireOp",EDGE,"0e071c30-8112-48db-a0b7-94a150164aee.sketch_text.stroke-17"),sQuery(id+"F44.wireOp",EDGE,"0e071c30-8112-48db-a0b7-94a150164aee.sketch_text.stroke-18"),sQuery(id+"F44.wireOp",EDGE,"0e071c30-8112-48db-a0b7-94a150164aee.sketch_text.stroke-19"),sQuery(id+"F44.wireOp",EDGE,"0e071c30-8112-48db-a0b7-94a150164aee.sketch_text.stroke-28"),sQuery(id+"F44.wireOp",EDGE,"0e071c30-8112-48db-a0b7-94a150164aee.sketch_text.stroke-29"),sQuery(id+"F44.wireOp",EDGE,"0e071c30-8112-48db-a0b7-94a150164aee.sketch_text.stroke-30"),sQuery(id+"F44.wireOp",EDGE,"0e071c30-8112-48db-a0b7-94a150164aee.sketch_text.stroke-31"),sQuery(id+"F44.wireOp",EDGE,"0e071c30-8112-48db-a0b7-94a150164aee.sketch_text.stroke-32"),sQuery(id+"F44.wireOp",EDGE,"0e071c30-8112-48db-a0b7-94a150164aee.sketch_text.stroke-33"),sQuery(id+"F44.wireOp",EDGE,"0e071c30-8112-48db-a0b7-94a150164aee.sketch_text.stroke-34"),sQuery(id+"F44.wireOp",EDGE,"0e071c30-8112-48db-a0b7-94a150164aee.sketch_text.stroke-35"),sQuery(id+"F44.wireOp",EDGE,"e2d7af9a-f6d1-4b82-89d6-a8a0b8d7c55a.sketch_text.stroke-0"),sQuery(id+"F44.wireOp",EDGE,"e2d7af9a-f6d1-4b82-89d6-a8a0b8d7c55a.sketch_text.stroke-1"),sQuery(id+"F44.wireOp",EDGE,"e2d7af9a-f6d1-4b82-89d6-a8a0b8d7c55a.sketch_text.stroke-2"),sQuery(id+"F44.wireOp",EDGE,"e2d7af9a-f6d1-4b82-89d6-a8a0b8d7c55a.sketch_text.stroke-3"),sQuery(id+"F44.wireOp",EDGE,"e2d7af9a-f6d1-4b82-89d6-a8a0b8d7c55a.sketch_text.stroke-4"),sQuery(id+"F44.wireOp",EDGE,"e2d7af9a-f6d1-4b82-89d6-a8a0b8d7c55a.sketch_text.stroke-5"),sQuery(id+"F44.wireOp",EDGE,"e2d7af9a-f6d1-4b82-89d6-a8a0b8d7c55a.sketch_text.stroke-6"),sQuery(id+"F44.wireOp",EDGE,"e2d7af9a-f6d1-4b82-89d6-a8a0b8d7c55a.sketch_text.stroke-7"),sQuery(id+"F44.wireOp",EDGE,"e2d7af9a-f6d1-4b82-89d6-a8a0b8d7c55a.sketch_text.stroke-8"),sQuery(id+"F44.wireOp",EDGE,"e2d7af9a-f6d1-4b82-89d6-a8a0b8d7c55a.sketch_text.stroke-9"),sQuery(id+"F44.wireOp",EDGE,"e2d7af9a-f6d1-4b82-89d6-a8a0b8d7c55a.sketch_text.stroke-10"),sQuery(id+"F44.wireOp",EDGE,"e2d7af9a-f6d1-4b82-89d6-a8a0b8d7c55a.sketch_text.stroke-11"),sQuery(id+"F44.wireOp",EDGE,"e2d7af9a-f6d1-4b82-89d6-a8a0b8d7c55a.sketch_text.stroke-12"),sQuery(id+"F44.wireOp",EDGE,"e2d7af9a-f6d1-4b82-89d6-a8a0b8d7c55a.sketch_text.stroke-13"),sQuery(id+"F44.wireOp",EDGE,"e2d7af9a-f6d1-4b82-89d6-a8a0b8d7c55a.sketch_text.stroke-14"),sQuery(id+"F44.wireOp",EDGE,"e2d7af9a-f6d1-4b82-89d6-a8a0b8d7c55a.sketch_text.stroke-15"),sQuery(id+"F44.wireOp",EDGE,"e2d7af9a-f6d1-4b82-89d6-a8a0b8d7c55a.sketch_text.stroke-16"),sQuery(id+"F44.wireOp",EDGE,"e2d7af9a-f6d1-4b82-89d6-a8a0b8d7c55a.sketch_text.stroke-17"),sQuery(id+"F44.wireOp",EDGE,"e2d7af9a-f6d1-4b82-89d6-a8a0b8d7c55a.sketch_text.stroke-18"),sQuery(id+"F44.wireOp",EDGE,"e2d7af9a-f6d1-4b82-89d6-a8a0b8d7c55a.sketch_text.stroke-19"),sQuery(id+"F44.wireOp",EDGE,"e2d7af9a-f6d1-4b82-89d6-a8a0b8d7c55a.sketch_text.stroke-20"),sQuery(id+"F44.wireOp",EDGE,"e2d7af9a-f6d1-4b82-89d6-a8a0b8d7c55a.sketch_text.stroke-21"),sQuery(id+"F44.wireOp",EDGE,"e2d7af9a-f6d1-4b82-89d6-a8a0b8d7c55a.sketch_text.stroke-22"),sQuery(id+"F44.wireOp",EDGE,"e2d7af9a-f6d1-4b82-89d6-a8a0b8d7c55a.sketch_text.stroke-31"),sQuery(id+"F44.wireOp",EDGE,"e2d7af9a-f6d1-4b82-89d6-a8a0b8d7c55a.sketch_text.stroke-32"),sQuery(id+"F44.wireOp",EDGE,"e2d7af9a-f6d1-4b82-89d6-a8a0b8d7c55a.sketch_text.stroke-33"),sQuery(id+"F44.wireOp",EDGE,"e2d7af9a-f6d1-4b82-89d6-a8a0b8d7c55a.sketch_text.stroke-34"),sQuery(id+"F44.wireOp",EDGE,"e2d7af9a-f6d1-4b82-89d6-a8a0b8d7c55a.sketch_text.stroke-35"),sQuery(id+"F44.wireOp",EDGE,"e2d7af9a-f6d1-4b82-89d6-a8a0b8d7c55a.sketch_text.stroke-36"),sQuery(id+"F44.wireOp",EDGE,"e2d7af9a-f6d1-4b82-89d6-a8a0b8d7c55a.sketch_text.stroke-37"),sQuery(id+"F44.wireOp",EDGE,"e2d7af9a-f6d1-4b82-89d6-a8a0b8d7c55a.sketch_text.stroke-38"),sQuery(id+"F44.wireOp",EDGE,"e2d7af9a-f6d1-4b82-89d6-a8a0b8d7c55a.sketch_text.stroke-39"),sQuery(id+"F44.wireOp",EDGE,"e2d7af9a-f6d1-4b82-89d6-a8a0b8d7c55a.sketch_text.stroke-40"),sQuery(id+"F44.wireOp",EDGE,"e2d7af9a-f6d1-4b82-89d6-a8a0b8d7c55a.sketch_text.stroke-41"),sQuery(id+"F44.wireOp",EDGE,"e2d7af9a-f6d1-4b82-89d6-a8a0b8d7c55a.sketch_text.stroke-42"),sQuery(id+"F44.wireOp",EDGE,"e2d7af9a-f6d1-4b82-89d6-a8a0b8d7c55a.sketch_text.stroke-43"),sQuery(id+"F44.wireOp",EDGE,"6fba481b-f54a-40dc-850f-529da61e2d5d.sketch_text.stroke-0"),sQuery(id+"F44.wireOp",EDGE,"6fba481b-f54a-40dc-850f-529da61e2d5d.sketch_text.stroke-1"),sQuery(id+"F44.wireOp",EDGE,"6fba481b-f54a-40dc-850f-529da61e2d5d.sketch_text.stroke-2"),sQuery(id+"F44.wireOp",EDGE,"6fba481b-f54a-40dc-850f-529da61e2d5d.sketch_text.stroke-3"),sQuery(id+"F44.wireOp",EDGE,"6fba481b-f54a-40dc-850f-529da61e2d5d.sketch_text.stroke-4"),sQuery(id+"F44.wireOp",EDGE,"6fba481b-f54a-40dc-850f-529da61e2d5d.sketch_text.stroke-5"),sQuery(id+"F44.wireOp",EDGE,"6fba481b-f54a-40dc-850f-529da61e2d5d.sketch_text.stroke-6"),sQuery(id+"F44.wireOp",EDGE,"6fba481b-f54a-40dc-850f-529da61e2d5d.sketch_text.stroke-7"),sQuery(id+"F44.wireOp",EDGE,"6fba481b-f54a-40dc-850f-529da61e2d5d.sketch_text.stroke-8"),sQuery(id+"F44.wireOp",EDGE,"6fba481b-f54a-40dc-850f-529da61e2d5d.sketch_text.stroke-9"),sQuery(id+"F44.wireOp",EDGE,"6fba481b-f54a-40dc-850f-529da61e2d5d.sketch_text.stroke-10"),sQuery(id+"F44.wireOp",EDGE,"6fba481b-f54a-40dc-850f-529da61e2d5d.sketch_text.stroke-11"),sQuery(id+"F44.wireOp",EDGE,"6fba481b-f54a-40dc-850f-529da61e2d5d.sketch_text.stroke-12"),sQuery(id+"F44.wireOp",EDGE,"6fba481b-f54a-40dc-850f-529da61e2d5d.sketch_text.stroke-13"),sQuery(id+"F44.wireOp",EDGE,"6fba481b-f54a-40dc-850f-529da61e2d5d.sketch_text.stroke-22"),sQuery(id+"F44.wireOp",EDGE,"6fba481b-f54a-40dc-850f-529da61e2d5d.sketch_text.stroke-23"),sQuery(id+"F44.wireOp",EDGE,"6fba481b-f54a-40dc-850f-529da61e2d5d.sketch_text.stroke-24"),sQuery(id+"F44.wireOp",EDGE,"6fba481b-f54a-40dc-850f-529da61e2d5d.sketch_text.stroke-25"),sQuery(id+"F44.wireOp",EDGE,"6fba481b-f54a-40dc-850f-529da61e2d5d.sketch_text.stroke-26"),sQuery(id+"F44.wireOp",EDGE,"6fba481b-f54a-40dc-850f-529da61e2d5d.sketch_text.stroke-27"),sQuery(id+"F44.wireOp",EDGE,"6fba481b-f54a-40dc-850f-529da61e2d5d.sketch_text.stroke-28"),sQuery(id+"F44.wireOp",EDGE,"6fba481b-f54a-40dc-850f-529da61e2d5d.sketch_text.stroke-29"),sQuery(id+"F44.wireOp",EDGE,"6fba481b-f54a-40dc-850f-529da61e2d5d.sketch_text.stroke-30"),sQuery(id+"F44.wireOp",EDGE,"6fba481b-f54a-40dc-850f-529da61e2d5d.sketch_text.stroke-31"),sQuery(id+"F44.wireOp",EDGE,"6fba481b-f54a-40dc-850f-529da61e2d5d.sketch_text.stroke-32"),sQuery(id+"F44.wireOp",EDGE,"6fba481b-f54a-40dc-850f-529da61e2d5d.sketch_text.stroke-33"),sQuery(id+"F44.wireOp",EDGE,"6fba481b-f54a-40dc-850f-529da61e2d5d.sketch_text.stroke-34"),sQuery(id+"F44.wireOp",EDGE,"6fba481b-f54a-40dc-850f-529da61e2d5d.sketch_text.stroke-35"),sQuery(id+"F44.wireOp",EDGE,"6fba481b-f54a-40dc-850f-529da61e2d5d.sketch_text.stroke-36"),sQuery(id+"F44.wireOp",EDGE,"6fba481b-f54a-40dc-850f-529da61e2d5d.sketch_text.stroke-37"),sQuery(id+"F44.wireOp",EDGE,"6fba481b-f54a-40dc-850f-529da61e2d5d.sketch_text.stroke-38"),sQuery(id+"F44.wireOp",EDGE,"6fba481b-f54a-40dc-850f-529da61e2d5d.sketch_text.stroke-39"),sQuery(id+"F44.wireOp",EDGE,"6fba481b-f54a-40dc-850f-529da61e2d5d.sketch_text.stroke-40"),sQuery(id+"F44.wireOp",EDGE,"6fba481b-f54a-40dc-850f-529da61e2d5d.sketch_text.stroke-41"),sQuery(id+"F44.wireOp",EDGE,"6fba481b-f54a-40dc-850f-529da61e2d5d.sketch_text.stroke-42"),sQuery(id+"F44.wireOp",EDGE,"6fba481b-f54a-40dc-850f-529da61e2d5d.sketch_text.stroke-43"),sQuery(id+"F44.wireOp",EDGE,"6fba481b-f54a-40dc-850f-529da61e2d5d.sketch_text.stroke-44"),sQuery(id+"F44.wireOp",EDGE,"6fba481b-f54a-40dc-850f-529da61e2d5d.sketch_text.stroke-45"),sQuery(id+"F44.wireOp",EDGE,"6fba481b-f54a-40dc-850f-529da61e2d5d.sketch_text.stroke-46"),sQuery(id+"F44.wireOp",EDGE,"6fba481b-f54a-40dc-850f-529da61e2d5d.sketch_text.stroke-47"),sQuery(id+"F44.wireOp",EDGE,"6fba481b-f54a-40dc-850f-529da61e2d5d.sketch_text.stroke-48"),sQuery(id+"F44.wireOp",EDGE,"6fba481b-f54a-40dc-850f-529da61e2d5d.sketch_text.stroke-49")])],"isStart":false})]});}
            extrude(context, id + "F46", {"entities" : qUnion([Q0]), "endBound" : BoundingType.UP_TO_SURFACE, "depth" : 25 * mm, "endBoundEntityFace" : qUnion([Q1]), "offsetDistance" : 25 * mm});
        }
        {
            var Q0;
            Q0=makeQuery(id+"F44.imprint","IMPRINT",FACE,{"disambiguationData":[TD([[makeQuery(id+"F44.imprint","IMPRINT",EDGE,{"derivedFrom":sQuery(id+"F44.wireOp",EDGE,"E202.bottom")}),-1.0]])]});
            var Q1;
            {var subQ0=sQuery(id+"F0.wireOp",EDGE,"E0.right");var subQ1=sQuery(id+"F0.wireOp",EDGE,"E0.bottom");var subQ2=sQuery(id+"F0.wireOp",EDGE,"E1");var subQ4=sQuery(id+"F0.wireOp",EDGE,"E0.left");Q1=makeQuery(id+"F45.boolean.opBoolean","MERGE",FACE,{"derivedFrom":[makeQuery(id+"F6.boolean.opBoolean","SPLIT",FACE,{"disambiguationData":[TD([makeQuery(id+"F1.opExtrude","CAP_FACE",FACE,{"disambiguationData":[OSD([subQ1,sQuery(id+"F0.wireOp",EDGE,"E0.top"),subQ4,subQ0,subQ2])],"isStart":false})])],"derivedFrom":makeQuery(id+"F1.opExtrude","SWEPT_FACE",FACE,{"disambiguationData":[OSD([subQ2])]})}),makeQuery(id+"F45.opExtrude","CAP_FACE",FACE,{"disambiguationData":[OSD([sQuery(id+"F44.wireOp",EDGE,"E200.bottom"),sQuery(id+"F44.wireOp",EDGE,"E200.top"),sQuery(id+"F44.wireOp",EDGE,"E200.left"),sQuery(id+"F44.wireOp",EDGE,"E200.right"),sQuery(id+"F44.wireOp",EDGE,"E201.bottom"),sQuery(id+"F44.wireOp",EDGE,"E201.top"),sQuery(id+"F44.wireOp",EDGE,"E201.left"),sQuery(id+"F44.wireOp",EDGE,"E201.right"),sQuery(id+"F44.wireOp",EDGE,"E202.bottom"),sQuery(id+"F44.wireOp",EDGE,"E202.top"),sQuery(id+"F44.wireOp",EDGE,"E202.left"),sQuery(id+"F44.wireOp",EDGE,"E202.right"),sQuery(id+"F44.wireOp",EDGE,"0e071c30-8112-48db-a0b7-94a150164aee.sketch_text.stroke-0"),sQuery(id+"F44.wireOp",EDGE,"0e071c30-8112-48db-a0b7-94a150164aee.sketch_text.stroke-1"),sQuery(id+"F44.wireOp",EDGE,"0e071c30-8112-48db-a0b7-94a150164aee.sketch_text.stroke-2"),sQuery(id+"F44.wireOp",EDGE,"0e071c30-8112-48db-a0b7-94a150164aee.sketch_text.stroke-3"),sQuery(id+"F44.wireOp",EDGE,"0e071c30-8112-48db-a0b7-94a150164aee.sketch_text.stroke-4"),sQuery(id+"F44.wireOp",EDGE,"0e071c30-8112-48db-a0b7-94a150164aee.sketch_text.stroke-5"),sQuery(id+"F44.wireOp",EDGE,"0e071c30-8112-48db-a0b7-94a150164aee.sketch_text.stroke-6"),sQuery(id+"F44.wireOp",EDGE,"0e071c30-8112-48db-a0b7-94a150164aee.sketch_text.stroke-7"),sQuery(id+"F44.wireOp",EDGE,"0e071c30-8112-48db-a0b7-94a150164aee.sketch_text.stroke-8"),sQuery(id+"F44.wireOp",EDGE,"0e071c30-8112-48db-a0b7-94a150164aee.sketch_text.stroke-9"),sQuery(id+"F44.wireOp",EDGE,"0e071c30-8112-48db-a0b7-94a150164aee.sketch_text.stroke-10"),sQuery(id+"F44.wireOp",EDGE,"0e071c30-8112-48db-a0b7-94a150164aee.sketch_text.stroke-11"),sQuery(id+"F44.wireOp",EDGE,"0e071c30-8112-48db-a0b7-94a150164aee.sketch_text.stroke-12"),sQuery(id+"F44.wireOp",EDGE,"0e071c30-8112-48db-a0b7-94a150164aee.sketch_text.stroke-13"),sQuery(id+"F44.wireOp",EDGE,"0e071c30-8112-48db-a0b7-94a150164aee.sketch_text.stroke-14"),sQuery(id+"F44.wireOp",EDGE,"0e071c30-8112-48db-a0b7-94a150164aee.sketch_text.stroke-15"),sQuery(id+"F44.wireOp",EDGE,"0e071c30-8112-48db-a0b7-94a150164aee.sketch_text.stroke-16"),sQuery(id+"F44.wireOp",EDGE,"0e071c30-8112-48db-a0b7-94a150164aee.sketch_text.stroke-17"),sQuery(id+"F44.wireOp",EDGE,"0e071c30-8112-48db-a0b7-94a150164aee.sketch_text.stroke-18"),sQuery(id+"F44.wireOp",EDGE,"0e071c30-8112-48db-a0b7-94a150164aee.sketch_text.stroke-19"),sQuery(id+"F44.wireOp",EDGE,"0e071c30-8112-48db-a0b7-94a150164aee.sketch_text.stroke-28"),sQuery(id+"F44.wireOp",EDGE,"0e071c30-8112-48db-a0b7-94a150164aee.sketch_text.stroke-29"),sQuery(id+"F44.wireOp",EDGE,"0e071c30-8112-48db-a0b7-94a150164aee.sketch_text.stroke-30"),sQuery(id+"F44.wireOp",EDGE,"0e071c30-8112-48db-a0b7-94a150164aee.sketch_text.stroke-31"),sQuery(id+"F44.wireOp",EDGE,"0e071c30-8112-48db-a0b7-94a150164aee.sketch_text.stroke-32"),sQuery(id+"F44.wireOp",EDGE,"0e071c30-8112-48db-a0b7-94a150164aee.sketch_text.stroke-33"),sQuery(id+"F44.wireOp",EDGE,"0e071c30-8112-48db-a0b7-94a150164aee.sketch_text.stroke-34"),sQuery(id+"F44.wireOp",EDGE,"0e071c30-8112-48db-a0b7-94a150164aee.sketch_text.stroke-35"),sQuery(id+"F44.wireOp",EDGE,"e2d7af9a-f6d1-4b82-89d6-a8a0b8d7c55a.sketch_text.stroke-0"),sQuery(id+"F44.wireOp",EDGE,"e2d7af9a-f6d1-4b82-89d6-a8a0b8d7c55a.sketch_text.stroke-1"),sQuery(id+"F44.wireOp",EDGE,"e2d7af9a-f6d1-4b82-89d6-a8a0b8d7c55a.sketch_text.stroke-2"),sQuery(id+"F44.wireOp",EDGE,"e2d7af9a-f6d1-4b82-89d6-a8a0b8d7c55a.sketch_text.stroke-3"),sQuery(id+"F44.wireOp",EDGE,"e2d7af9a-f6d1-4b82-89d6-a8a0b8d7c55a.sketch_text.stroke-4"),sQuery(id+"F44.wireOp",EDGE,"e2d7af9a-f6d1-4b82-89d6-a8a0b8d7c55a.sketch_text.stroke-5"),sQuery(id+"F44.wireOp",EDGE,"e2d7af9a-f6d1-4b82-89d6-a8a0b8d7c55a.sketch_text.stroke-6"),sQuery(id+"F44.wireOp",EDGE,"e2d7af9a-f6d1-4b82-89d6-a8a0b8d7c55a.sketch_text.stroke-7"),sQuery(id+"F44.wireOp",EDGE,"e2d7af9a-f6d1-4b82-89d6-a8a0b8d7c55a.sketch_text.stroke-8"),sQuery(id+"F44.wireOp",EDGE,"e2d7af9a-f6d1-4b82-89d6-a8a0b8d7c55a.sketch_text.stroke-9"),sQuery(id+"F44.wireOp",EDGE,"e2d7af9a-f6d1-4b82-89d6-a8a0b8d7c55a.sketch_text.stroke-10"),sQuery(id+"F44.wireOp",EDGE,"e2d7af9a-f6d1-4b82-89d6-a8a0b8d7c55a.sketch_text.stroke-11"),sQuery(id+"F44.wireOp",EDGE,"e2d7af9a-f6d1-4b82-89d6-a8a0b8d7c55a.sketch_text.stroke-12"),sQuery(id+"F44.wireOp",EDGE,"e2d7af9a-f6d1-4b82-89d6-a8a0b8d7c55a.sketch_text.stroke-13"),sQuery(id+"F44.wireOp",EDGE,"e2d7af9a-f6d1-4b82-89d6-a8a0b8d7c55a.sketch_text.stroke-14"),sQuery(id+"F44.wireOp",EDGE,"e2d7af9a-f6d1-4b82-89d6-a8a0b8d7c55a.sketch_text.stroke-15"),sQuery(id+"F44.wireOp",EDGE,"e2d7af9a-f6d1-4b82-89d6-a8a0b8d7c55a.sketch_text.stroke-16"),sQuery(id+"F44.wireOp",EDGE,"e2d7af9a-f6d1-4b82-89d6-a8a0b8d7c55a.sketch_text.stroke-17"),sQuery(id+"F44.wireOp",EDGE,"e2d7af9a-f6d1-4b82-89d6-a8a0b8d7c55a.sketch_text.stroke-18"),sQuery(id+"F44.wireOp",EDGE,"e2d7af9a-f6d1-4b82-89d6-a8a0b8d7c55a.sketch_text.stroke-19"),sQuery(id+"F44.wireOp",EDGE,"e2d7af9a-f6d1-4b82-89d6-a8a0b8d7c55a.sketch_text.stroke-20"),sQuery(id+"F44.wireOp",EDGE,"e2d7af9a-f6d1-4b82-89d6-a8a0b8d7c55a.sketch_text.stroke-21"),sQuery(id+"F44.wireOp",EDGE,"e2d7af9a-f6d1-4b82-89d6-a8a0b8d7c55a.sketch_text.stroke-22"),sQuery(id+"F44.wireOp",EDGE,"e2d7af9a-f6d1-4b82-89d6-a8a0b8d7c55a.sketch_text.stroke-31"),sQuery(id+"F44.wireOp",EDGE,"e2d7af9a-f6d1-4b82-89d6-a8a0b8d7c55a.sketch_text.stroke-32"),sQuery(id+"F44.wireOp",EDGE,"e2d7af9a-f6d1-4b82-89d6-a8a0b8d7c55a.sketch_text.stroke-33"),sQuery(id+"F44.wireOp",EDGE,"e2d7af9a-f6d1-4b82-89d6-a8a0b8d7c55a.sketch_text.stroke-34"),sQuery(id+"F44.wireOp",EDGE,"e2d7af9a-f6d1-4b82-89d6-a8a0b8d7c55a.sketch_text.stroke-35"),sQuery(id+"F44.wireOp",EDGE,"e2d7af9a-f6d1-4b82-89d6-a8a0b8d7c55a.sketch_text.stroke-36"),sQuery(id+"F44.wireOp",EDGE,"e2d7af9a-f6d1-4b82-89d6-a8a0b8d7c55a.sketch_text.stroke-37"),sQuery(id+"F44.wireOp",EDGE,"e2d7af9a-f6d1-4b82-89d6-a8a0b8d7c55a.sketch_text.stroke-38"),sQuery(id+"F44.wireOp",EDGE,"e2d7af9a-f6d1-4b82-89d6-a8a0b8d7c55a.sketch_text.stroke-39"),sQuery(id+"F44.wireOp",EDGE,"e2d7af9a-f6d1-4b82-89d6-a8a0b8d7c55a.sketch_text.stroke-40"),sQuery(id+"F44.wireOp",EDGE,"e2d7af9a-f6d1-4b82-89d6-a8a0b8d7c55a.sketch_text.stroke-41"),sQuery(id+"F44.wireOp",EDGE,"e2d7af9a-f6d1-4b82-89d6-a8a0b8d7c55a.sketch_text.stroke-42"),sQuery(id+"F44.wireOp",EDGE,"e2d7af9a-f6d1-4b82-89d6-a8a0b8d7c55a.sketch_text.stroke-43"),sQuery(id+"F44.wireOp",EDGE,"6fba481b-f54a-40dc-850f-529da61e2d5d.sketch_text.stroke-0"),sQuery(id+"F44.wireOp",EDGE,"6fba481b-f54a-40dc-850f-529da61e2d5d.sketch_text.stroke-1"),sQuery(id+"F44.wireOp",EDGE,"6fba481b-f54a-40dc-850f-529da61e2d5d.sketch_text.stroke-2"),sQuery(id+"F44.wireOp",EDGE,"6fba481b-f54a-40dc-850f-529da61e2d5d.sketch_text.stroke-3"),sQuery(id+"F44.wireOp",EDGE,"6fba481b-f54a-40dc-850f-529da61e2d5d.sketch_text.stroke-4"),sQuery(id+"F44.wireOp",EDGE,"6fba481b-f54a-40dc-850f-529da61e2d5d.sketch_text.stroke-5"),sQuery(id+"F44.wireOp",EDGE,"6fba481b-f54a-40dc-850f-529da61e2d5d.sketch_text.stroke-6"),sQuery(id+"F44.wireOp",EDGE,"6fba481b-f54a-40dc-850f-529da61e2d5d.sketch_text.stroke-7"),sQuery(id+"F44.wireOp",EDGE,"6fba481b-f54a-40dc-850f-529da61e2d5d.sketch_text.stroke-8"),sQuery(id+"F44.wireOp",EDGE,"6fba481b-f54a-40dc-850f-529da61e2d5d.sketch_text.stroke-9"),sQuery(id+"F44.wireOp",EDGE,"6fba481b-f54a-40dc-850f-529da61e2d5d.sketch_text.stroke-10"),sQuery(id+"F44.wireOp",EDGE,"6fba481b-f54a-40dc-850f-529da61e2d5d.sketch_text.stroke-11"),sQuery(id+"F44.wireOp",EDGE,"6fba481b-f54a-40dc-850f-529da61e2d5d.sketch_text.stroke-12"),sQuery(id+"F44.wireOp",EDGE,"6fba481b-f54a-40dc-850f-529da61e2d5d.sketch_text.stroke-13"),sQuery(id+"F44.wireOp",EDGE,"6fba481b-f54a-40dc-850f-529da61e2d5d.sketch_text.stroke-22"),sQuery(id+"F44.wireOp",EDGE,"6fba481b-f54a-40dc-850f-529da61e2d5d.sketch_text.stroke-23"),sQuery(id+"F44.wireOp",EDGE,"6fba481b-f54a-40dc-850f-529da61e2d5d.sketch_text.stroke-24"),sQuery(id+"F44.wireOp",EDGE,"6fba481b-f54a-40dc-850f-529da61e2d5d.sketch_text.stroke-25"),sQuery(id+"F44.wireOp",EDGE,"6fba481b-f54a-40dc-850f-529da61e2d5d.sketch_text.stroke-26"),sQuery(id+"F44.wireOp",EDGE,"6fba481b-f54a-40dc-850f-529da61e2d5d.sketch_text.stroke-27"),sQuery(id+"F44.wireOp",EDGE,"6fba481b-f54a-40dc-850f-529da61e2d5d.sketch_text.stroke-28"),sQuery(id+"F44.wireOp",EDGE,"6fba481b-f54a-40dc-850f-529da61e2d5d.sketch_text.stroke-29"),sQuery(id+"F44.wireOp",EDGE,"6fba481b-f54a-40dc-850f-529da61e2d5d.sketch_text.stroke-30"),sQuery(id+"F44.wireOp",EDGE,"6fba481b-f54a-40dc-850f-529da61e2d5d.sketch_text.stroke-31"),sQuery(id+"F44.wireOp",EDGE,"6fba481b-f54a-40dc-850f-529da61e2d5d.sketch_text.stroke-32"),sQuery(id+"F44.wireOp",EDGE,"6fba481b-f54a-40dc-850f-529da61e2d5d.sketch_text.stroke-33"),sQuery(id+"F44.wireOp",EDGE,"6fba481b-f54a-40dc-850f-529da61e2d5d.sketch_text.stroke-34"),sQuery(id+"F44.wireOp",EDGE,"6fba481b-f54a-40dc-850f-529da61e2d5d.sketch_text.stroke-35"),sQuery(id+"F44.wireOp",EDGE,"6fba481b-f54a-40dc-850f-529da61e2d5d.sketch_text.stroke-36"),sQuery(id+"F44.wireOp",EDGE,"6fba481b-f54a-40dc-850f-529da61e2d5d.sketch_text.stroke-37"),sQuery(id+"F44.wireOp",EDGE,"6fba481b-f54a-40dc-850f-529da61e2d5d.sketch_text.stroke-38"),sQuery(id+"F44.wireOp",EDGE,"6fba481b-f54a-40dc-850f-529da61e2d5d.sketch_text.stroke-39"),sQuery(id+"F44.wireOp",EDGE,"6fba481b-f54a-40dc-850f-529da61e2d5d.sketch_text.stroke-40"),sQuery(id+"F44.wireOp",EDGE,"6fba481b-f54a-40dc-850f-529da61e2d5d.sketch_text.stroke-41"),sQuery(id+"F44.wireOp",EDGE,"6fba481b-f54a-40dc-850f-529da61e2d5d.sketch_text.stroke-42"),sQuery(id+"F44.wireOp",EDGE,"6fba481b-f54a-40dc-850f-529da61e2d5d.sketch_text.stroke-43"),sQuery(id+"F44.wireOp",EDGE,"6fba481b-f54a-40dc-850f-529da61e2d5d.sketch_text.stroke-44"),sQuery(id+"F44.wireOp",EDGE,"6fba481b-f54a-40dc-850f-529da61e2d5d.sketch_text.stroke-45"),sQuery(id+"F44.wireOp",EDGE,"6fba481b-f54a-40dc-850f-529da61e2d5d.sketch_text.stroke-46"),sQuery(id+"F44.wireOp",EDGE,"6fba481b-f54a-40dc-850f-529da61e2d5d.sketch_text.stroke-47"),sQuery(id+"F44.wireOp",EDGE,"6fba481b-f54a-40dc-850f-529da61e2d5d.sketch_text.stroke-48"),sQuery(id+"F44.wireOp",EDGE,"6fba481b-f54a-40dc-850f-529da61e2d5d.sketch_text.stroke-49")])],"isStart":false})]});}
            extrude(context, id + "F47", {"entities" : qUnion([Q0]), "endBound" : BoundingType.UP_TO_SURFACE, "depth" : 25 * mm, "endBoundEntityFace" : qUnion([Q1]), "offsetDistance" : 25 * mm});
        }
    });
